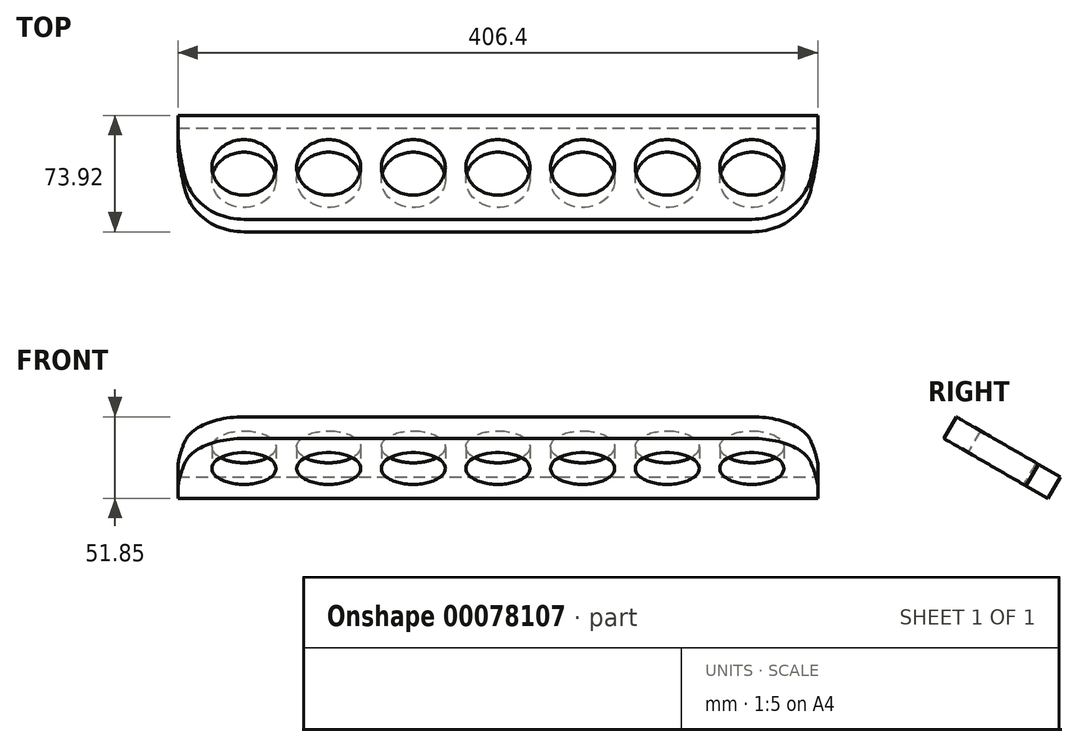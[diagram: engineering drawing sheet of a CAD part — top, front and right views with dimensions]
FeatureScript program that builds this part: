
annotation { "Feature Type Name" : "Feature", "Feature Type Description" : "" }
export const myFeature = defineFeature(function(context is Context, id is Id, definition is map)
    precondition{}
    {
        {
            assignVariable(context, id + "F0", {"name" : "panel_length", "anyValue" : 48});
        }
        {
            assignVariable(context, id + "F1", {"name" : "ply_thk", "anyValue" : 5 / 8});
        }
        {
            assignVariable(context, id + "F2", {"name" : "washer_thk", "anyValue" : 1 / 16});
        }
        {
            var Q0;
            Q0=qCreatedBy(makeId("Right.planeOp"),FACE);
            var sketch = newSketch(context, id + "F3", { "sketchPlane" : qUnion([Q0])});
            skCircle(sketch, "E0", {"center": v(0, 0) * mm, "radius": 254 * mm, "construction": true});
            skLineSegment(sketch, "E1", {"start": v(-651.77, -620.9) * mm, "end": v(0, 508) * mm, "construction": true});
            skCircle(sketch, "E2", {"center": v(0, 381) * mm, "radius": 63.5 * mm, "construction": true});
            skPoint(sketch, "E3", {"position": v(-219.97, 127) * mm});
            skPoint(sketch, "E4", {"position": v(-245.37, 83) * mm});
            skCircle(sketch, "E5", {"center": v(0, 254) * mm, "radius": 127 * mm, "construction": true});
            skLineSegment(sketch, "E6", {"start": v(-1219.2, 0) * mm, "end": v(1219.2, 0) * mm, "construction": true});
            skLineSegment(sketch, "E7", {"start": v(0, 1219.2) * mm, "end": v(0, -1219.2) * mm, "construction": true});
            skLineSegment(sketch, "E8", {"start": v(-245.37, 83) * mm, "end": v(-231.62, 75.07) * mm, "construction": true});
            skLineSegment(sketch, "E9", {"start": v(-231.62, 75.07) * mm, "end": v(-638.02, -628.84) * mm, "construction": true});
            skLineSegment(sketch, "E10", {"start": v(-638.02, -628.84) * mm, "end": v(-651.77, -620.9) * mm, "construction": true});
            skLineSegment(sketch, "E11", {"start": v(-231.62, 75.07) * mm, "end": v(-217.87, 67.13) * mm, "construction": true});
            skLineSegment(sketch, "E12", {"start": v(-217.87, 67.13) * mm, "end": v(-624.27, -636.77) * mm, "construction": true});
            skLineSegment(sketch, "E13", {"start": v(-624.27, -636.77) * mm, "end": v(-638.02, -628.84) * mm, "construction": true});
            skCircle(sketch, "E14", {"center": v(0, 0) * mm, "radius": 6.35 * mm, "construction": true});
            skCircle(sketch, "E15", {"center": v(0, 0) * mm, "radius": 9.53 * mm, "construction": true});
            skPoint(sketch, "E16", {"position": v(-55, 412.75) * mm});
            skPoint(sketch, "E17", {"position": v(-109.99, 317.5) * mm});
            skCircle(sketch, "E18", {"center": v(0, 0) * mm, "radius": 177.8 * mm, "construction": true});
            skCircle(sketch, "E19", {"center": v(0, 508) * mm, "radius": 6.35 * mm});
            skCircle(sketch, "E20", {"center": v(0, 508) * mm, "radius": 9.53 * mm});
            skCircle(sketch, "E21", {"center": v(0, 508) * mm, "radius": 12.7 * mm});
            skSolve(sketch);
        }
        {
            var Q0;
            Q0=qCreatedBy(makeId("Right.planeOp"),FACE);
            var sketch = newSketch(context, id + "F4", { "sketchPlane" : qUnion([Q0])});
            skArc(sketch, "E22", {"start": v(-98.09, -220.46) * mm, "mid": v(-82.53, -226.75) * mm, "end": v(-66.57, -231.93) * mm});
            skArc(sketch, "E23", {"start": v(-209.94, -413.28) * mm, "mid": v(-158.54, -435.6) * mm, "end": v(-104.83, -451.54) * mm});
            skArc(sketch, "E24", {"start": v(-248.13, -450.54) * mm, "mid": v(-175.92, -483.33) * mm, "end": v(-99.53, -504.63) * mm});
            skArc(sketch, "E25", {"start": v(-365.54, -639.5) * mm, "mid": v(-251.93, -692.18) * mm, "end": v(-131.05, -724.85) * mm});
            skLineSegment(sketch, "E26", {"start": v(160.85, -238.47) * mm, "end": v(229.05, -339.58) * mm});
            skLineSegment(sketch, "E27", {"start": v(-237.79, -697.16) * mm, "end": v(-166.04, -486.81) * mm, "construction": true});
            skLineSegment(sketch, "E28", {"start": v(-149.64, -438.73) * mm, "end": v(-77.9, -228.38) * mm, "construction": true});
            skLineSegment(sketch, "E29", {"start": v(30.07, -286.07) * mm, "end": v(42.82, -407.37) * mm});
            skLineSegment(sketch, "E30.0", {"start": v(0, 1219.2) * mm, "end": v(0, -1219.2) * mm, "construction": true});
            skLineSegment(sketch, "E31.MirrorCS", {"start": v(-30.07, -286.07) * mm, "end": v(-42.82, -407.37) * mm});
            skLineSegment(sketch, "E32.MirrorCS", {"start": v(-160.85, -238.47) * mm, "end": v(-229.05, -339.58) * mm});
            skLineSegment(sketch, "E33.0", {"start": v(-1219.2, 0) * mm, "end": v(1219.2, 0) * mm, "construction": true});
            skArc(sketch, "E34.trimOffspring", {"start": v(131.05, -724.85) * mm, "mid": v(251.93, -692.18) * mm, "end": v(365.54, -639.5) * mm});
            skArc(sketch, "E35.trimOffspring", {"start": v(99.53, -504.63) * mm, "mid": v(175.92, -483.33) * mm, "end": v(248.13, -450.54) * mm});
            skArc(sketch, "E36.trimOffspring", {"start": v(104.83, -451.54) * mm, "mid": v(158.54, -435.6) * mm, "end": v(209.94, -413.28) * mm});
            skArc(sketch, "E37.trimOffspring", {"start": v(66.57, -231.93) * mm, "mid": v(82.53, -226.75) * mm, "end": v(98.09, -220.46) * mm});
            skLineSegment(sketch, "E38.trimOffspring", {"start": v(58.84, -559.78) * mm, "end": v(71.49, -680.17) * mm});
            skLineSegment(sketch, "E39.trimOffspring", {"start": v(314.75, -466.63) * mm, "end": v(382.44, -567) * mm});
            skLineSegment(sketch, "E40.trimOffspring", {"start": v(-314.75, -466.63) * mm, "end": v(-382.44, -567) * mm});
            skLineSegment(sketch, "E41.trimOffspring", {"start": v(-58.84, -559.78) * mm, "end": v(-71.49, -680.17) * mm});
            skPoint(sketch, "E42.visualSharp", {"position": v(-134.93, -200.05) * mm});
            skArc(sketch, "E42.filletArc", {"start": v(-98.09, -220.46) * mm, "mid": v(-132.74, -218.05) * mm, "end": v(-160.85, -238.47) * mm});
            skPoint(sketch, "E43.visualSharp", {"position": v(-25.22, -239.98) * mm});
            skArc(sketch, "E43.filletArc", {"start": v(-30.07, -286.07) * mm, "mid": v(-38.47, -252.36) * mm, "end": v(-66.57, -231.93) * mm});
            skPoint(sketch, "E44.visualSharp", {"position": v(25.22, -239.98) * mm});
            skArc(sketch, "E44.filletArc", {"start": v(66.57, -231.93) * mm, "mid": v(38.47, -252.36) * mm, "end": v(30.07, -286.07) * mm});
            skPoint(sketch, "E45.visualSharp", {"position": v(134.93, -200.05) * mm});
            skArc(sketch, "E45.filletArc", {"start": v(160.85, -238.47) * mm, "mid": v(132.74, -218.05) * mm, "end": v(98.09, -220.46) * mm});
            skPoint(sketch, "E46.visualSharp", {"position": v(-259.21, -384.3) * mm});
            skArc(sketch, "E46.filletArc", {"start": v(-229.05, -339.58) * mm, "mid": v(-236.11, -380.74) * mm, "end": v(-209.94, -413.28) * mm});
            skPoint(sketch, "E47.visualSharp", {"position": v(-48.45, -461.01) * mm});
            skArc(sketch, "E47.filletArc", {"start": v(-104.83, -451.54) * mm, "mid": v(-63.86, -443.43) * mm, "end": v(-42.82, -407.37) * mm});
            skPoint(sketch, "E48.visualSharp", {"position": v(48.45, -461.01) * mm});
            skArc(sketch, "E48.filletArc", {"start": v(42.82, -407.37) * mm, "mid": v(63.86, -443.43) * mm, "end": v(104.83, -451.54) * mm});
            skPoint(sketch, "E49.visualSharp", {"position": v(259.21, -384.3) * mm});
            skArc(sketch, "E49.filletArc", {"start": v(209.94, -413.28) * mm, "mid": v(236.11, -380.74) * mm, "end": v(229.05, -339.58) * mm});
            skPoint(sketch, "E50.visualSharp", {"position": v(-411.9, -610.67) * mm});
            skArc(sketch, "E50.filletArc", {"start": v(-382.44, -567) * mm, "mid": v(-389.8, -606.93) * mm, "end": v(-365.54, -639.5) * mm});
            skPoint(sketch, "E51.visualSharp", {"position": v(-287.62, -426.42) * mm});
            skArc(sketch, "E51.filletArc", {"start": v(-248.13, -450.54) * mm, "mid": v(-284.56, -445.66) * mm, "end": v(-314.75, -466.63) * mm});
            skPoint(sketch, "E52.visualSharp", {"position": v(-53.76, -511.53) * mm});
            skArc(sketch, "E52.filletArc", {"start": v(-58.84, -559.78) * mm, "mid": v(-68.48, -524.3) * mm, "end": v(-99.53, -504.63) * mm});
            skPoint(sketch, "E53.visualSharp", {"position": v(-77, -732.56) * mm});
            skArc(sketch, "E53.filletArc", {"start": v(-131.05, -724.85) * mm, "mid": v(-91.53, -715.5) * mm, "end": v(-71.49, -680.17) * mm});
            skPoint(sketch, "E54.visualSharp", {"position": v(77, -732.56) * mm});
            skArc(sketch, "E54.filletArc", {"start": v(71.49, -680.17) * mm, "mid": v(91.53, -715.5) * mm, "end": v(131.05, -724.85) * mm});
            skPoint(sketch, "E55.visualSharp", {"position": v(53.76, -511.53) * mm});
            skArc(sketch, "E55.filletArc", {"start": v(99.53, -504.63) * mm, "mid": v(68.48, -524.3) * mm, "end": v(58.84, -559.78) * mm});
            skPoint(sketch, "E56.visualSharp", {"position": v(287.62, -426.42) * mm});
            skArc(sketch, "E56.filletArc", {"start": v(314.75, -466.63) * mm, "mid": v(284.56, -445.66) * mm, "end": v(248.13, -450.54) * mm});
            skPoint(sketch, "E57.visualSharp", {"position": v(411.9, -610.67) * mm});
            skArc(sketch, "E57.filletArc", {"start": v(365.54, -639.5) * mm, "mid": v(389.8, -606.93) * mm, "end": v(382.44, -567) * mm});
            skSolve(sketch);
        }
        {
            var Q0;
            Q0=makeQuery(id+"F3.imprint","IMPRINT",FACE,{"disambiguationData":[TD([[makeQuery(id+"F3.imprint","IMPRINT",EDGE,{"derivedFrom":sQuery(id+"F3.wireOp",EDGE,"E20")}),-1.0]])]});
            var Q1;
            Q1=makeQuery(id+"F3.imprint","IMPRINT",FACE,{"disambiguationData":[TD([[makeQuery(id+"F3.imprint","IMPRINT",EDGE,{"derivedFrom":sQuery(id+"F3.wireOp",EDGE,"E19")}),-1.0]])]});
            extrude(context, id + "F5", {"entities" : qUnion([Q0, Q1]), "depth" : (getVariable(context, 'washer_thk')) * mm});
        }
        {
            var Q0;
            Q0=makeQuery(id+"F3.imprint","IMPRINT",FACE,{"disambiguationData":[TD([[makeQuery(id+"F3.imprint","IMPRINT",EDGE,{"derivedFrom":sQuery(id+"F3.wireOp",EDGE,"E19")}),-1.0]])]});
            extrude(context, id + "F6", {"entities" : qUnion([Q0]), "depth" : (getVariable(context, 'ply_thk')) * mm});
        }
        {
            var Q0;
            Q0=makeQuery(id+"F3.imprint","IMPRINT",FACE,{"disambiguationData":[TD([[makeQuery(id+"F3.imprint","IMPRINT",EDGE,{"derivedFrom":sQuery(id+"F3.wireOp",EDGE,"E19")}),1.0]])]});
            extrude(context, id + "F7", {"entities" : qUnion([Q0]), "depth" : (getVariable(context, 'panel_length')) * mm});
        }
        {
            var Q0;
            Q0=qCreatedBy(makeId("Right.planeOp"),FACE);
            var sketch = newSketch(context, id + "F8", { "sketchPlane" : qUnion([Q0])});
            skCircle(sketch, "E58.0", {"center": v(0, 0) * mm, "radius": 254 * mm, "construction": true});
            skLineSegment(sketch, "E58.1", {"start": v(-217.87, 67.13) * mm, "end": v(-624.27, -636.77) * mm, "construction": true});
            skLineSegment(sketch, "E58.2", {"start": v(-231.62, 75.07) * mm, "end": v(-217.87, 67.13) * mm, "construction": true});
            skLineSegment(sketch, "E58.3", {"start": v(-231.62, 75.07) * mm, "end": v(-638.02, -628.84) * mm, "construction": true});
            skLineSegment(sketch, "E58.4", {"start": v(-624.27, -636.77) * mm, "end": v(-638.02, -628.84) * mm, "construction": true});
            skCircle(sketch, "E59", {"center": v(0, 0) * mm, "radius": 127 * mm, "construction": true});
            skCircle(sketch, "E60.0", {"center": v(0, 0) * mm, "radius": 177.8 * mm, "construction": true});
            skLineSegment(sketch, "E61", {"start": v(-212.37, 63.96) * mm, "end": v(-121.6, 36.62) * mm});
            skLineSegment(sketch, "E62", {"start": v(-212.37, 63.96) * mm, "end": v(-574.32, -562.96) * mm});
            skCircle(sketch, "E63", {"center": v(-535.83, -585.18) * mm, "radius": 44.45 * mm, "construction": true});
            skLineSegment(sketch, "E64.0", {"start": v(0, 1219.2) * mm, "end": v(0, -1219.2) * mm, "construction": true});
            skCircle(sketch, "E65", {"center": v(0, 0) * mm, "radius": 793.45 * mm, "construction": true});
            skCircle(sketch, "E66", {"center": v(-535.83, -585.18) * mm, "radius": 9.53 * mm, "construction": true});
            skCircle(sketch, "E67.MirrorC", {"center": v(455.1, -649.95) * mm, "radius": 44.45 * mm, "construction": true});
            skCircle(sketch, "E68.MirrorC", {"center": v(535.83, -585.18) * mm, "radius": 44.45 * mm, "construction": true});
            skCircle(sketch, "E69.MirrorC", {"center": v(455.1, -649.95) * mm, "radius": 9.53 * mm});
            skCircle(sketch, "E70.MirrorC", {"center": v(535.83, -585.18) * mm, "radius": 9.53 * mm, "construction": true});
            skLineSegment(sketch, "E71", {"start": v(-535.83, -585.18) * mm, "end": v(-421.53, -387.21) * mm, "construction": true});
            skLineSegment(sketch, "E72", {"start": v(-544.08, -580.42) * mm, "end": v(-429.78, -382.45) * mm});
            skCircle(sketch, "E73", {"center": v(-421.53, -387.21) * mm, "radius": 9.53 * mm, "construction": true});
            skLineSegment(sketch, "E74.MirrorCS", {"start": v(-527.58, -589.95) * mm, "end": v(-413.28, -391.97) * mm});
            skCircle(sketch, "E75", {"center": v(-218.33, -35.26) * mm, "radius": 44.45 * mm, "construction": true});
            skArc(sketch, "E76", {"start": v(-574.32, -562.96) * mm, "mid": v(-557.56, -623.96) * mm, "end": v(-496.78, -606.42) * mm});
            skArc(sketch, "E77", {"start": v(-496.78, -606.42) * mm, "mid": v(-51.13, -782.25) * mm, "end": v(413.62, -665.92) * mm});
            skArc(sketch, "E78", {"start": v(413.62, -665.92) * mm, "mid": v(473.92, -690.22) * mm, "end": v(493.97, -628.38) * mm});
            skArc(sketch, "E79", {"start": v(111.05, 61.63) * mm, "mid": v(-13.57, 126.27) * mm, "end": v(-121.6, 36.62) * mm});
            skArc(sketch, "E80", {"start": v(-544.08, -580.42) * mm, "mid": v(-540.6, -593.43) * mm, "end": v(-527.58, -589.95) * mm});
            skArc(sketch, "E81", {"start": v(-413.28, -391.97) * mm, "mid": v(-416.77, -378.96) * mm, "end": v(-429.78, -382.45) * mm});
            skCircle(sketch, "E82", {"center": v(-218.33, -35.26) * mm, "radius": 9.53 * mm});
            skCircle(sketch, "E83", {"center": v(0, 0) * mm, "radius": 9.53 * mm});
            skCircle(sketch, "E84", {"center": v(0, -127) * mm, "radius": 9.52 * mm, "construction": true});
            skCircle(sketch, "E85", {"center": v(0, 0) * mm, "radius": 837.9 * mm, "construction": true});
            skLineSegment(sketch, "E86", {"start": v(-1330.3, -888.7) * mm, "end": v(1330.3, -888.7) * mm, "construction": true});
            skPoint(sketch, "E87", {"position": v(0, -888.7) * mm});
            skCircle(sketch, "E88", {"center": v(63.5, -109.99) * mm, "radius": 9.53 * mm, "construction": true});
            skArc(sketch, "E89", {"start": v(0, -136.53) * mm, "mid": v(35.34, -131.87) * mm, "end": v(68.26, -118.23) * mm});
            skArc(sketch, "E90", {"start": v(0, -117.47) * mm, "mid": v(30.4, -113.47) * mm, "end": v(58.74, -101.74) * mm});
            skArc(sketch, "E91", {"start": v(0, -117.47) * mm, "mid": v(-9.52, -127) * mm, "end": v(0, -136.53) * mm});
            skArc(sketch, "E92", {"start": v(68.26, -118.23) * mm, "mid": v(71.75, -105.22) * mm, "end": v(58.74, -101.74) * mm});
            skLineSegment(sketch, "E93", {"start": v(493.97, -628.38) * mm, "end": v(111.05, 61.63) * mm});
            skCircle(sketch, "E94.MirrorC", {"center": v(218.33, -35.26) * mm, "radius": 9.53 * mm, "construction": true});
            skCircle(sketch, "E95.MirrorC", {"center": v(421.53, -387.21) * mm, "radius": 9.53 * mm, "construction": true});
            skLineSegment(sketch, "E96", {"start": v(0, 0) * mm, "end": v(63.5, -109.99) * mm, "construction": true});
            skCircle(sketch, "E97", {"center": v(0, -793.45) * mm, "radius": 6.35 * mm, "construction": true});
            skLineSegment(sketch, "E98", {"start": v(0, 0) * mm, "end": v(69.15, -790.43) * mm, "construction": true});
            skLineSegment(sketch, "E99", {"start": v(0, 0) * mm, "end": v(455.1, -649.95) * mm, "construction": true});
            skCircle(sketch, "E100", {"center": v(69.15, -790.43) * mm, "radius": 44.45 * mm, "construction": true});
            skLineSegment(sketch, "E101", {"start": v(-143.55, 168.8) * mm, "end": v(-78.6, 99.75) * mm, "construction": true});
            skLineSegment(sketch, "E102", {"start": v(-78.6, 99.75) * mm, "end": v(0, 0) * mm, "construction": true});
            skLineSegment(sketch, "E103", {"start": v(-121.6, 36.62) * mm, "end": v(0, 0) * mm, "construction": true});
            skArc(sketch, "E104", {"start": v(82.97, 104.4) * mm, "mid": v(0, 133.35) * mm, "end": v(-82.97, 104.4) * mm});
            skLineSegment(sketch, "E105", {"start": v(-113.5, 136.86) * mm, "end": v(-82.97, 104.4) * mm});
            skLineSegment(sketch, "E106.MirrorCS", {"start": v(113.5, 136.86) * mm, "end": v(82.97, 104.4) * mm});
            skArc(sketch, "E107", {"start": v(113.5, 136.86) * mm, "mid": v(0, 177.8) * mm, "end": v(-113.5, 136.86) * mm});
            skCircle(sketch, "E108", {"center": v(-52.13, 146.57) * mm, "radius": 6.35 * mm});
            skArc(sketch, "E109", {"start": v(0, 155.57) * mm, "mid": v(-52.13, 146.57) * mm, "end": v(-98.24, 120.62) * mm, "construction": true});
            skCircle(sketch, "E110.MirrorC", {"center": v(52.13, 146.57) * mm, "radius": 6.35 * mm});
            skCircle(sketch, "E111", {"center": v(0, -793.45) * mm, "radius": 9.53 * mm, "construction": true});
            skLineSegment(sketch, "E112.2.0", {"start": v(-98.09, -220.46) * mm, "end": v(-98.09, -220.46) * mm});
            skLineSegment(sketch, "E112.3.0", {"start": v(-248.13, -450.54) * mm, "end": v(-248.13, -450.54) * mm});
            skArc(sketch, "E113.1.0", {"start": v(-66.57, -231.93) * mm, "mid": v(-82.53, -226.75) * mm, "end": v(-98.09, -220.46) * mm});
            skArc(sketch, "E113.1.1", {"start": v(-98.09, -220.46) * mm, "mid": v(-132.74, -218.05) * mm, "end": v(-160.85, -238.47) * mm});
            skLineSegment(sketch, "E113.1.2", {"start": v(-160.85, -238.47) * mm, "end": v(-229.05, -339.58) * mm});
            skArc(sketch, "E113.1.3", {"start": v(-229.05, -339.58) * mm, "mid": v(-236.11, -380.74) * mm, "end": v(-209.94, -413.28) * mm});
            skArc(sketch, "E113.1.4", {"start": v(-209.94, -413.28) * mm, "mid": v(-158.54, -435.6) * mm, "end": v(-104.83, -451.54) * mm});
            skArc(sketch, "E113.1.5", {"start": v(-104.83, -451.54) * mm, "mid": v(-63.86, -443.43) * mm, "end": v(-42.82, -407.37) * mm});
            skLineSegment(sketch, "E113.1.6", {"start": v(-42.82, -407.37) * mm, "end": v(-30.07, -286.07) * mm});
            skArc(sketch, "E113.1.7", {"start": v(-30.07, -286.07) * mm, "mid": v(-38.47, -252.36) * mm, "end": v(-66.57, -231.93) * mm});
            skLineSegment(sketch, "E113.2.0", {"start": v(229.05, -339.58) * mm, "end": v(160.85, -238.47) * mm});
            skArc(sketch, "E113.2.1", {"start": v(160.85, -238.47) * mm, "mid": v(132.74, -218.05) * mm, "end": v(98.09, -220.46) * mm});
            skArc(sketch, "E113.2.2", {"start": v(98.09, -220.46) * mm, "mid": v(82.53, -226.75) * mm, "end": v(66.57, -231.93) * mm});
            skArc(sketch, "E113.2.3", {"start": v(66.57, -231.93) * mm, "mid": v(38.47, -252.36) * mm, "end": v(30.07, -286.07) * mm});
            skLineSegment(sketch, "E113.2.4", {"start": v(30.07, -286.07) * mm, "end": v(42.82, -407.37) * mm});
            skArc(sketch, "E113.2.5", {"start": v(42.82, -407.37) * mm, "mid": v(63.86, -443.43) * mm, "end": v(104.83, -451.54) * mm});
            skArc(sketch, "E113.2.6", {"start": v(104.83, -451.54) * mm, "mid": v(158.54, -435.6) * mm, "end": v(209.94, -413.28) * mm});
            skArc(sketch, "E113.2.7", {"start": v(209.94, -413.28) * mm, "mid": v(236.11, -380.74) * mm, "end": v(229.05, -339.58) * mm});
            skArc(sketch, "E113.3.0", {"start": v(71.49, -680.17) * mm, "mid": v(91.53, -715.5) * mm, "end": v(131.05, -724.85) * mm});
            skArc(sketch, "E113.3.1", {"start": v(131.05, -724.85) * mm, "mid": v(231.68, -699.22) * mm, "end": v(327.7, -659.7) * mm});
            skLineSegment(sketch, "E113.3.3", {"start": v(373.43, -553.63) * mm, "end": v(314.75, -466.63) * mm});
            skArc(sketch, "E113.3.4", {"start": v(314.75, -466.63) * mm, "mid": v(284.56, -445.66) * mm, "end": v(248.13, -450.54) * mm});
            skArc(sketch, "E113.3.5", {"start": v(248.13, -450.54) * mm, "mid": v(202.04, -473) * mm, "end": v(153.94, -490.77) * mm});
            skLineSegment(sketch, "E113.3.7", {"start": v(60.51, -575.76) * mm, "end": v(71.49, -680.17) * mm});
            skLineSegment(sketch, "E114", {"start": v(154.76, -539.49) * mm, "end": v(345.6, -592.31) * mm});
            skLineSegment(sketch, "E115", {"start": v(323.18, -612.46) * mm, "end": v(92.55, -548.62) * mm});
            skArc(sketch, "E116", {"start": v(365.54, -639.5) * mm, "mid": v(388.99, -625.52) * mm, "end": v(411.9, -610.67) * mm, "construction": true});
            skLineSegment(sketch, "E117", {"start": v(382.44, -567) * mm, "end": v(411.9, -610.67) * mm, "construction": true});
            skArc(sketch, "E118", {"start": v(53.76, -511.53) * mm, "mid": v(76.72, -508.6) * mm, "end": v(99.53, -504.63) * mm, "construction": true});
            skLineSegment(sketch, "E119", {"start": v(53.76, -511.53) * mm, "end": v(58.84, -559.78) * mm, "construction": true});
            skPoint(sketch, "E120.newPointB", {"position": v(365.54, -639.5) * mm});
            skArc(sketch, "E120.filletArc", {"start": v(327.7, -659.7) * mm, "mid": v(341.68, -634.52) * mm, "end": v(323.18, -612.46) * mm});
            skPoint(sketch, "E121.newPointB", {"position": v(382.44, -567) * mm});
            skArc(sketch, "E121.filletArc", {"start": v(345.6, -592.31) * mm, "mid": v(372.99, -582.67) * mm, "end": v(373.43, -553.63) * mm});
            skPoint(sketch, "E122.newPointB", {"position": v(99.53, -504.63) * mm});
            skArc(sketch, "E122.filletArc", {"start": v(153.94, -490.77) * mm, "mid": v(136.14, -515.44) * mm, "end": v(154.76, -539.49) * mm});
            skPoint(sketch, "E123.newPointB", {"position": v(58.84, -559.78) * mm});
            skArc(sketch, "E123.filletArc", {"start": v(92.55, -548.62) * mm, "mid": v(69.36, -553.72) * mm, "end": v(60.51, -575.76) * mm});
            skLineSegment(sketch, "E124", {"start": v(53.76, -511.53) * mm, "end": v(411.9, -610.67) * mm, "construction": true});
            skArc(sketch, "E125.MirrorCS", {"start": v(-92.55, -548.62) * mm, "mid": v(-69.36, -553.72) * mm, "end": v(-60.51, -575.76) * mm});
            skLineSegment(sketch, "E126.MirrorCS", {"start": v(-60.51, -575.76) * mm, "end": v(-71.49, -680.17) * mm});
            skArc(sketch, "E127.MirrorCS", {"start": v(-71.49, -680.17) * mm, "mid": v(-91.53, -715.5) * mm, "end": v(-131.05, -724.85) * mm});
            skArc(sketch, "E128.MirrorCS", {"start": v(-131.05, -724.85) * mm, "mid": v(-231.68, -699.22) * mm, "end": v(-327.7, -659.7) * mm});
            skArc(sketch, "E129.MirrorCS", {"start": v(-327.7, -659.7) * mm, "mid": v(-341.68, -634.52) * mm, "end": v(-323.18, -612.46) * mm});
            skLineSegment(sketch, "E130.MirrorCS", {"start": v(-323.18, -612.46) * mm, "end": v(-92.55, -548.62) * mm});
            skArc(sketch, "E131.MirrorCS", {"start": v(-153.94, -490.77) * mm, "mid": v(-136.14, -515.44) * mm, "end": v(-154.76, -539.49) * mm});
            skArc(sketch, "E132.MirrorCS", {"start": v(-248.13, -450.54) * mm, "mid": v(-202.04, -473) * mm, "end": v(-153.94, -490.77) * mm});
            skArc(sketch, "E133.MirrorCS", {"start": v(-314.75, -466.63) * mm, "mid": v(-284.56, -445.66) * mm, "end": v(-248.13, -450.54) * mm});
            skLineSegment(sketch, "E134.MirrorCS", {"start": v(-373.43, -553.63) * mm, "end": v(-314.75, -466.63) * mm});
            skArc(sketch, "E135.MirrorCS", {"start": v(-345.6, -592.31) * mm, "mid": v(-372.99, -582.67) * mm, "end": v(-373.43, -553.63) * mm});
            skLineSegment(sketch, "E136.MirrorCS", {"start": v(-154.76, -539.49) * mm, "end": v(-345.6, -592.31) * mm});
            skSolve(sketch);
        }
        {
            var Q0;
            Q0=qCreatedBy(makeId("Right.planeOp"),FACE);
            var sketch = newSketch(context, id + "F9", { "sketchPlane" : qUnion([Q0])});
            skCircle(sketch, "E137.0", {"center": v(-535.83, -585.18) * mm, "radius": 9.53 * mm, "construction": true});
            skCircle(sketch, "E137.1", {"center": v(-421.53, -387.21) * mm, "radius": 9.53 * mm, "construction": true});
            skCircle(sketch, "E137.2", {"center": v(0, -793.45) * mm, "radius": 9.53 * mm, "construction": true});
            skCircle(sketch, "E137.3", {"center": v(0, -127) * mm, "radius": 9.52 * mm, "construction": true});
            skCircle(sketch, "E137.4", {"center": v(63.5, -109.99) * mm, "radius": 9.53 * mm, "construction": true});
            skCircle(sketch, "E137.5", {"center": v(455.1, -649.95) * mm, "radius": 9.53 * mm, "construction": true});
            skCircle(sketch, "E137.6", {"center": v(69.15, -790.43) * mm, "radius": 44.45 * mm, "construction": true});
            skCircle(sketch, "E138.0", {"center": v(-218.33, -35.26) * mm, "radius": 9.53 * mm, "construction": true});
            skCircle(sketch, "E139", {"center": v(0, -793.45) * mm, "radius": 25.4 * mm, "construction": true});
            skCircle(sketch, "E140", {"center": v(69.15, -790.43) * mm, "radius": 25.4 * mm, "construction": true});
            skCircle(sketch, "E141", {"center": v(455.1, -649.95) * mm, "radius": 25.4 * mm, "construction": true});
            skCircle(sketch, "E142", {"center": v(-535.83, -585.18) * mm, "radius": 25.4 * mm, "construction": true});
            skCircle(sketch, "E143", {"center": v(-421.53, -387.21) * mm, "radius": 25.4 * mm, "construction": true});
            skCircle(sketch, "E144", {"center": v(-218.33, -35.26) * mm, "radius": 25.4 * mm, "construction": true});
            skCircle(sketch, "E145", {"center": v(0, -127) * mm, "radius": 25.4 * mm, "construction": true});
            skCircle(sketch, "E146", {"center": v(63.5, -109.99) * mm, "radius": 25.4 * mm, "construction": true});
            skLineSegment(sketch, "E147", {"start": v(-25.4, -127) * mm, "end": v(-25.4, -793.45) * mm});
            skCircle(sketch, "E148.0", {"center": v(0, 0) * mm, "radius": 127 * mm, "construction": true});
            skArc(sketch, "E149", {"start": v(0, -101.6) * mm, "mid": v(26.3, -98.14) * mm, "end": v(50.8, -87.99) * mm});
            skArc(sketch, "E150", {"start": v(0, -101.6) * mm, "mid": v(-17.96, -109.04) * mm, "end": v(-25.4, -127) * mm});
            skLineSegment(sketch, "E151", {"start": v(85.5, -97.29) * mm, "end": v(405.8, -652.08) * mm});
            skArc(sketch, "E152", {"start": v(85.5, -97.29) * mm, "mid": v(70.07, -85.45) * mm, "end": v(50.8, -87.99) * mm});
            skArc(sketch, "E153", {"start": v(0, -818.85) * mm, "mid": v(246.23, -780.95) * mm, "end": v(469.67, -670.76) * mm});
            skArc(sketch, "E154", {"start": v(-25.4, -793.45) * mm, "mid": v(-17.96, -811.4) * mm, "end": v(0, -818.85) * mm});
            skArc(sketch, "E155", {"start": v(405.8, -652.08) * mm, "mid": v(423.33, -640.85) * mm, "end": v(440.53, -629.15) * mm});
            skArc(sketch, "E156", {"start": v(469.67, -670.76) * mm, "mid": v(475.9, -635.38) * mm, "end": v(440.53, -629.15) * mm});
            skCircle(sketch, "E157", {"center": v(0, 0) * mm, "radius": 25.4 * mm, "construction": true});
            skLineSegment(sketch, "E158", {"start": v(-4.05, 25.08) * mm, "end": v(-222.38, -10.18) * mm});
            skLineSegment(sketch, "E159", {"start": v(-240.33, -22.56) * mm, "end": v(-557.83, -572.48) * mm});
            skLineSegment(sketch, "E160", {"start": v(-513.83, -597.88) * mm, "end": v(-202.37, -58.4) * mm});
            skLineSegment(sketch, "E161", {"start": v(-202.37, -58.4) * mm, "end": v(4.05, -25.08) * mm});
            skArc(sketch, "E162", {"start": v(4.05, -25.08) * mm, "mid": v(25.08, 4.05) * mm, "end": v(-4.05, 25.08) * mm});
            skArc(sketch, "E163", {"start": v(-222.38, -10.18) * mm, "mid": v(-232.75, -14.35) * mm, "end": v(-240.33, -22.56) * mm});
            skArc(sketch, "E164", {"start": v(-557.83, -572.48) * mm, "mid": v(-548.53, -607.18) * mm, "end": v(-513.83, -597.88) * mm});
            skLineSegment(sketch, "E165", {"start": v(-224.28, -33.03) * mm, "end": v(-446.94, -627.3) * mm, "construction": true});
            skLineSegment(sketch, "E166", {"start": v(-464.78, -620.6) * mm, "end": v(-429.1, -633.98) * mm});
            skCircle(sketch, "E167", {"center": v(-494.5, -656.65) * mm, "radius": 38.1 * mm, "construction": true});
            skLineSegment(sketch, "E168", {"start": v(-429.1, -633.98) * mm, "end": v(-424.98, -658.73) * mm});
            skLineSegment(sketch, "E169", {"start": v(-443.98, -601.28) * mm, "end": v(-398.3, -479.38) * mm});
            skLineSegment(sketch, "E170", {"start": v(-386.4, -483.84) * mm, "end": v(-432.08, -605.74) * mm});
            skLineSegment(sketch, "E171", {"start": v(-443.98, -601.28) * mm, "end": v(-441.6, -602.17) * mm});
            skLineSegment(sketch, "E172", {"start": v(-441.6, -602.17) * mm, "end": v(-450.5, -625.96) * mm});
            skLineSegment(sketch, "E173", {"start": v(-443.37, -628.63) * mm, "end": v(-434.46, -604.85) * mm});
            skLineSegment(sketch, "E174", {"start": v(-434.46, -604.85) * mm, "end": v(-432.08, -605.74) * mm});
            skLineSegment(sketch, "E175", {"start": v(-441.6, -602.17) * mm, "end": v(-438.03, -603.5) * mm, "construction": true});
            skLineSegment(sketch, "E176", {"start": v(-438.03, -603.5) * mm, "end": v(-434.46, -604.85) * mm, "construction": true});
            skLineSegment(sketch, "E177", {"start": v(-398.3, -479.38) * mm, "end": v(-395.92, -480.27) * mm});
            skLineSegment(sketch, "E178", {"start": v(-386.4, -483.84) * mm, "end": v(-388.79, -482.95) * mm});
            skLineSegment(sketch, "E179", {"start": v(-388.79, -482.95) * mm, "end": v(-384.33, -471.05) * mm});
            skLineSegment(sketch, "E180", {"start": v(-395.92, -480.27) * mm, "end": v(-391.47, -468.38) * mm});
            skCircle(sketch, "E181", {"center": v(-218.33, -35.26) * mm, "radius": 6.35 * mm, "construction": true});
            skCircle(sketch, "E182.0", {"center": v(0, -793.45) * mm, "radius": 6.35 * mm, "construction": true});
            skLineSegment(sketch, "E183", {"start": v(-6.27, -794.46) * mm, "end": v(-140.41, 33.57) * mm, "construction": true});
            skLineSegment(sketch, "E184", {"start": v(-159.22, 30.53) * mm, "end": v(-121.6, 36.62) * mm});
            skPoint(sketch, "E185", {"position": v(-446.94, -627.3) * mm});
            skLineSegment(sketch, "E186", {"start": v(-464.78, -620.6) * mm, "end": v(-471.58, -626.21) * mm});
            skLineSegment(sketch, "E187", {"start": v(-144.17, 32.97) * mm, "end": v(-117.77, -130) * mm});
            skLineSegment(sketch, "E188", {"start": v(-136.65, 34.18) * mm, "end": v(-110.25, -128.8) * mm});
            skLineSegment(sketch, "E189", {"start": v(-110.25, -128.8) * mm, "end": v(-107.74, -128.39) * mm});
            skLineSegment(sketch, "E190", {"start": v(-117.77, -130) * mm, "end": v(-120.28, -130.42) * mm});
            skLineSegment(sketch, "E191", {"start": v(-117.77, -130) * mm, "end": v(-114, -129.4) * mm, "construction": true});
            skLineSegment(sketch, "E192", {"start": v(-114, -129.4) * mm, "end": v(-110.25, -128.8) * mm, "construction": true});
            skLineSegment(sketch, "E193", {"start": v(-159.22, 30.53) * mm, "end": v(-178.05, 53.62) * mm});
            skLineSegment(sketch, "E194", {"start": v(-99.46, -258.92) * mm, "end": v(-120.28, -130.42) * mm});
            skLineSegment(sketch, "E195", {"start": v(-86.92, -256.88) * mm, "end": v(-107.74, -128.39) * mm});
            skLineSegment(sketch, "E196", {"start": v(-391.47, -468.38) * mm, "end": v(-395.03, -467.04) * mm});
            skLineSegment(sketch, "E197", {"start": v(-395.03, -467.04) * mm, "end": v(-339.33, -318.39) * mm});
            skLineSegment(sketch, "E198", {"start": v(-325.06, -323.73) * mm, "end": v(-380.76, -472.4) * mm});
            skLineSegment(sketch, "E199", {"start": v(-380.76, -472.4) * mm, "end": v(-384.33, -471.05) * mm});
            skLineSegment(sketch, "E200", {"start": v(-339.33, -318.39) * mm, "end": v(-335.77, -319.72) * mm});
            skLineSegment(sketch, "E201", {"start": v(-335.77, -319.72) * mm, "end": v(-303.47, -233.52) * mm});
            skLineSegment(sketch, "E202", {"start": v(-280.28, -193.37) * mm, "end": v(-328.63, -322.4) * mm});
            skLineSegment(sketch, "E203", {"start": v(-328.63, -322.4) * mm, "end": v(-325.06, -323.73) * mm});
            skLineSegment(sketch, "E204", {"start": v(-99.46, -258.92) * mm, "end": v(-96.95, -258.5) * mm});
            skLineSegment(sketch, "E205", {"start": v(-96.95, -258.5) * mm, "end": v(-94.92, -271.05) * mm});
            skLineSegment(sketch, "E206", {"start": v(-87.4, -269.83) * mm, "end": v(-89.43, -257.3) * mm});
            skLineSegment(sketch, "E207", {"start": v(-89.43, -257.3) * mm, "end": v(-86.92, -256.88) * mm});
            skLineSegment(sketch, "E208", {"start": v(-87.4, -269.83) * mm, "end": v(-83.64, -269.22) * mm});
            skLineSegment(sketch, "E209", {"start": v(-83.64, -269.22) * mm, "end": v(-58.25, -425.93) * mm});
            skLineSegment(sketch, "E210", {"start": v(-73.3, -428.36) * mm, "end": v(-98.68, -271.66) * mm});
            skLineSegment(sketch, "E211", {"start": v(-98.68, -271.66) * mm, "end": v(-94.92, -271.05) * mm});
            skLineSegment(sketch, "E212", {"start": v(-73.3, -428.36) * mm, "end": v(-69.53, -427.75) * mm});
            skLineSegment(sketch, "E213", {"start": v(-69.53, -427.75) * mm, "end": v(-25.4, -700.19) * mm});
            skLineSegment(sketch, "E214", {"start": v(-25.4, -652.54) * mm, "end": v(-62.01, -426.53) * mm});
            skLineSegment(sketch, "E215", {"start": v(-62.01, -426.53) * mm, "end": v(-58.25, -425.93) * mm});
            skArc(sketch, "E216", {"start": v(-471.58, -626.21) * mm, "mid": v(-471.07, -675.13) * mm, "end": v(-424.98, -658.73) * mm});
            skArc(sketch, "E217", {"start": v(-121.6, 36.62) * mm, "mid": v(-146.2, 57.17) * mm, "end": v(-178.05, 53.62) * mm});
            skSolve(sketch);
        }
        {
            var Q0;
            Q0=qCreatedBy(makeId("Right.planeOp"),FACE);
            var sketch = newSketch(context, id + "F10", { "sketchPlane" : qUnion([Q0])});
            skArc(sketch, "E218.0", {"start": v(82.6, -185.65) * mm, "mid": v(69.5, -190.95) * mm, "end": v(56.06, -195.31) * mm, "construction": true});
            skArc(sketch, "E218.1", {"start": v(192.44, -217.17) * mm, "mid": v(143.25, -181.43) * mm, "end": v(82.6, -185.65) * mm, "construction": true});
            skArc(sketch, "E218.2", {"start": v(56.06, -195.31) * mm, "mid": v(6.88, -231.06) * mm, "end": v(-7.82, -290.06) * mm, "construction": true});
            skLineSegment(sketch, "E218.3", {"start": v(260.64, -318.28) * mm, "end": v(192.44, -217.17) * mm, "construction": true});
            skLineSegment(sketch, "E218.4", {"start": v(-7.82, -290.06) * mm, "end": v(4.92, -411.35) * mm, "construction": true});
            skArc(sketch, "E218.5", {"start": v(4.92, -411.35) * mm, "mid": v(41.76, -474.46) * mm, "end": v(113.44, -488.66) * mm, "construction": true});
            skArc(sketch, "E218.6", {"start": v(113.44, -488.66) * mm, "mid": v(171.57, -471.4) * mm, "end": v(227.2, -447.25) * mm, "construction": true});
            skArc(sketch, "E218.7", {"start": v(227.2, -447.25) * mm, "mid": v(273, -390.3) * mm, "end": v(260.64, -318.28) * mm, "construction": true});
            skLineSegment(sketch, "E219.0", {"start": v(405.02, -532.33) * mm, "end": v(346.33, -445.33) * mm, "construction": true});
            skArc(sketch, "E219.1", {"start": v(229.75, -417.17) * mm, "mid": v(187.07, -437.97) * mm, "end": v(142.53, -454.42) * mm, "construction": true});
            skArc(sketch, "E219.2", {"start": v(142.53, -454.42) * mm, "mid": v(98.05, -516.09) * mm, "end": v(144.6, -576.2) * mm, "construction": true});
            skArc(sketch, "E219.3", {"start": v(346.33, -445.33) * mm, "mid": v(293.5, -408.63) * mm, "end": v(229.75, -417.17) * mm, "construction": true});
            skLineSegment(sketch, "E219.4", {"start": v(144.6, -576.2) * mm, "end": v(335.43, -629.03) * mm, "construction": true});
            skArc(sketch, "E219.5", {"start": v(335.43, -629.03) * mm, "mid": v(403.92, -604.92) * mm, "end": v(405.02, -532.33) * mm, "construction": true});
            skArc(sketch, "E220.0", {"start": v(344.65, -693.81) * mm, "mid": v(379.61, -630.89) * mm, "end": v(333.34, -575.74) * mm, "construction": true});
            skArc(sketch, "E220.1", {"start": v(102.72, -511.9) * mm, "mid": v(44.74, -524.65) * mm, "end": v(22.62, -579.74) * mm, "construction": true});
            skLineSegment(sketch, "E220.2", {"start": v(22.62, -579.74) * mm, "end": v(33.6, -684.15) * mm, "construction": true});
            skLineSegment(sketch, "E220.3", {"start": v(333.34, -575.74) * mm, "end": v(102.72, -511.9) * mm, "construction": true});
            skArc(sketch, "E220.4", {"start": v(33.6, -684.15) * mm, "mid": v(68.66, -745.97) * mm, "end": v(137.83, -762.34) * mm, "construction": true});
            skArc(sketch, "E220.5", {"start": v(137.83, -762.34) * mm, "mid": v(243.66, -735.38) * mm, "end": v(344.65, -693.81) * mm, "construction": true});
            skArc(sketch, "E221.0", {"start": v(0, -174.62) * mm, "mid": v(45.2, -168.67) * mm, "end": v(87.31, -151.23) * mm, "construction": true});
            skArc(sketch, "E221.1", {"start": v(0, -79.38) * mm, "mid": v(-47.62, -127) * mm, "end": v(0, -174.62) * mm, "construction": true});
            skArc(sketch, "E221.2", {"start": v(0, -79.38) * mm, "mid": v(20.54, -76.67) * mm, "end": v(39.69, -68.74) * mm, "construction": true});
            skArc(sketch, "E221.3", {"start": v(87.31, -151.23) * mm, "mid": v(104.74, -86.17) * mm, "end": v(39.69, -68.74) * mm, "construction": true});
            skCircle(sketch, "E222.0", {"center": v(0, 0) * mm, "radius": 47.62 * mm, "construction": true});
            skCircle(sketch, "E223.0", {"center": v(-218.33, -35.26) * mm, "radius": 47.62 * mm, "construction": true});
            skArc(sketch, "E224.0", {"start": v(-516.14, -538.38) * mm, "mid": v(-51.5, -744.04) * mm, "end": v(437.05, -604.34) * mm, "construction": true});
            skLineSegment(sketch, "E225.0", {"start": v(-194.47, 18.77) * mm, "end": v(-516.14, -538.38) * mm, "construction": true});
            skLineSegment(sketch, "E226.0", {"start": v(437.05, -604.34) * mm, "end": v(77.73, 43.14) * mm, "construction": true});
            skArc(sketch, "E226.1", {"start": v(77.73, 43.14) * mm, "mid": v(-28.68, 84.15) * mm, "end": v(-87.9, -13.32) * mm, "construction": true});
            skLineSegment(sketch, "E226.2", {"start": v(-194.47, 18.77) * mm, "end": v(-87.9, -13.32) * mm, "construction": true});
            skArc(sketch, "E227.0", {"start": v(-380.29, -411.02) * mm, "mid": v(-397.72, -345.97) * mm, "end": v(-462.77, -363.4) * mm, "construction": true});
            skLineSegment(sketch, "E227.1", {"start": v(-494.59, -609) * mm, "end": v(-380.29, -411.02) * mm, "construction": true});
            skArc(sketch, "E227.2", {"start": v(-577.07, -561.37) * mm, "mid": v(-559.64, -626.43) * mm, "end": v(-494.59, -609) * mm, "construction": true});
            skLineSegment(sketch, "E227.3", {"start": v(-577.07, -561.37) * mm, "end": v(-462.77, -363.4) * mm, "construction": true});
            skLineSegment(sketch, "E228.0", {"start": v(0, 1219.2) * mm, "end": v(0, -1219.2) * mm, "construction": true});
            skArc(sketch, "E229.MirrorCS", {"start": v(-4.92, -411.35) * mm, "mid": v(-41.76, -474.46) * mm, "end": v(-113.44, -488.66) * mm, "construction": true});
            skArc(sketch, "E230.MirrorCS", {"start": v(-113.44, -488.66) * mm, "mid": v(-171.57, -471.4) * mm, "end": v(-227.2, -447.25) * mm, "construction": true});
            skArc(sketch, "E231.MirrorCS", {"start": v(-227.2, -447.25) * mm, "mid": v(-273, -390.3) * mm, "end": v(-260.64, -318.28) * mm, "construction": true});
            skLineSegment(sketch, "E232.MirrorCS", {"start": v(-260.64, -318.28) * mm, "end": v(-192.44, -217.17) * mm, "construction": true});
            skArc(sketch, "E233.MirrorCS", {"start": v(-192.44, -217.17) * mm, "mid": v(-143.25, -181.43) * mm, "end": v(-82.6, -185.65) * mm, "construction": true});
            skArc(sketch, "E234.MirrorCS", {"start": v(-82.6, -185.65) * mm, "mid": v(-69.5, -190.95) * mm, "end": v(-56.06, -195.31) * mm, "construction": true});
            skArc(sketch, "E235.MirrorCS", {"start": v(-56.06, -195.31) * mm, "mid": v(-6.88, -231.06) * mm, "end": v(7.82, -290.06) * mm, "construction": true});
            skLineSegment(sketch, "E236.MirrorCS", {"start": v(7.82, -290.06) * mm, "end": v(-4.92, -411.35) * mm, "construction": true});
            skArc(sketch, "E237.MirrorCS", {"start": v(-142.53, -454.42) * mm, "mid": v(-98.05, -516.09) * mm, "end": v(-144.6, -576.2) * mm, "construction": true});
            skArc(sketch, "E238.MirrorCS", {"start": v(-229.75, -417.17) * mm, "mid": v(-187.07, -437.97) * mm, "end": v(-142.53, -454.42) * mm, "construction": true});
            skArc(sketch, "E239.MirrorCS", {"start": v(-346.33, -445.33) * mm, "mid": v(-293.5, -408.63) * mm, "end": v(-229.75, -417.17) * mm, "construction": true});
            skLineSegment(sketch, "E240.MirrorCS", {"start": v(-405.02, -532.33) * mm, "end": v(-346.33, -445.33) * mm, "construction": true});
            skArc(sketch, "E241.MirrorCS", {"start": v(-335.43, -629.03) * mm, "mid": v(-403.92, -604.92) * mm, "end": v(-405.02, -532.33) * mm, "construction": true});
            skLineSegment(sketch, "E242.MirrorCS", {"start": v(-144.6, -576.2) * mm, "end": v(-335.43, -629.03) * mm, "construction": true});
            skLineSegment(sketch, "E243.MirrorCS", {"start": v(-333.34, -575.74) * mm, "end": v(-102.72, -511.9) * mm, "construction": true});
            skArc(sketch, "E244.MirrorCS", {"start": v(-344.65, -693.81) * mm, "mid": v(-379.61, -630.89) * mm, "end": v(-333.34, -575.74) * mm, "construction": true});
            skArc(sketch, "E245.MirrorCS", {"start": v(-137.83, -762.34) * mm, "mid": v(-243.66, -735.38) * mm, "end": v(-344.65, -693.81) * mm, "construction": true});
            skArc(sketch, "E246.MirrorCS", {"start": v(-33.6, -684.15) * mm, "mid": v(-68.66, -745.97) * mm, "end": v(-137.83, -762.34) * mm, "construction": true});
            skLineSegment(sketch, "E247.MirrorCS", {"start": v(-22.62, -579.74) * mm, "end": v(-33.6, -684.15) * mm, "construction": true});
            skArc(sketch, "E248.MirrorCS", {"start": v(-102.72, -511.9) * mm, "mid": v(-44.74, -524.65) * mm, "end": v(-22.62, -579.74) * mm, "construction": true});
            skCircle(sketch, "E249", {"center": v(-256.1, -206) * mm, "radius": 59.02 * mm});
            skCircle(sketch, "E250", {"center": v(-329.12, -340.5) * mm, "radius": 55.92 * mm});
            skCircle(sketch, "E251", {"center": v(-118.99, -104.5) * mm, "radius": 73.47 * mm});
            skCircle(sketch, "E252", {"center": v(77.51, -28.57) * mm, "radius": 34.99 * mm});
            skCircle(sketch, "E253", {"center": v(140.14, -143.72) * mm, "radius": 36.1 * mm});
            skCircle(sketch, "E254", {"center": v(0, -502.05) * mm, "radius": 47.88 * mm});
            skCircle(sketch, "E255", {"center": v(0, -708.23) * mm, "radius": 37.6 * mm});
            skCircle(sketch, "E256", {"center": v(0, -199.9) * mm, "radius": 25.27 * mm});
            skCircle(sketch, "E257", {"center": v(294.07, -388.15) * mm, "radius": 20.12 * mm});
            skCircle(sketch, "E258", {"center": v(-441.62, -568.75) * mm, "radius": 25.75 * mm});
            skCircle(sketch, "E259", {"center": v(-375.27, -447.68) * mm, "radius": 22.67 * mm});
            skSolve(sketch);
        }
        {
            var Q0;
            Q0=makeQuery(id+"F8.imprint","IMPRINT",FACE,{"disambiguationData":[TD([[makeQuery(id+"F8.imprint","IMPRINT",EDGE,{"derivedFrom":sQuery(id+"F8.wireOp",EDGE,"E61")}),-1.0]])]});
            extrude(context, id + "F11", {"entities" : qUnion([Q0]), "depth" : (getVariable(context, 'ply_thk')) * mm});
        }
        {
            var Q0;
            Q0=makeQuery(id+"F8.imprint","IMPRINT",FACE,{"disambiguationData":[TD([[makeQuery(id+"F8.imprint","IMPRINT",EDGE,{"derivedFrom":sQuery(id+"F8.wireOp",EDGE,"E61")}),-1.0]])]});
            extrude(context, id + "F12", {"entities" : qUnion([Q0]), "oppositeDirection" : true, "depth" : (getVariable(context, 'ply_thk')) * mm});
        }
        {
            var Q0;
            Q0=makeQuery(id+"F10.imprint","IMPRINT",FACE,{"disambiguationData":[TD([[makeQuery(id+"F10.imprint","IMPRINT",EDGE,{"derivedFrom":sQuery(id+"F10.wireOp",EDGE,"E255")}),1.0]])]});
            var Q1;
            Q1=makeQuery(id+"F10.imprint","IMPRINT",FACE,{"disambiguationData":[TD([[makeQuery(id+"F10.imprint","IMPRINT",EDGE,{"derivedFrom":sQuery(id+"F10.wireOp",EDGE,"E254")}),1.0]])]});
            var Q2;
            Q2=makeQuery(id+"F10.imprint","IMPRINT",FACE,{"disambiguationData":[TD([[makeQuery(id+"F10.imprint","IMPRINT",EDGE,{"derivedFrom":sQuery(id+"F10.wireOp",EDGE,"E250")}),1.0]])]});
            var Q3;
            Q3=makeQuery(id+"F10.imprint","IMPRINT",FACE,{"disambiguationData":[TD([[makeQuery(id+"F10.imprint","IMPRINT",EDGE,{"derivedFrom":sQuery(id+"F10.wireOp",EDGE,"E249")}),1.0]])]});
            var Q4;
            Q4=makeQuery(id+"F10.imprint","IMPRINT",FACE,{"disambiguationData":[TD([[makeQuery(id+"F10.imprint","IMPRINT",EDGE,{"derivedFrom":sQuery(id+"F10.wireOp",EDGE,"E251")}),1.0]])]});
            var Q5;
            Q5=makeQuery(id+"F10.imprint","IMPRINT",FACE,{"disambiguationData":[TD([[makeQuery(id+"F10.imprint","IMPRINT",EDGE,{"derivedFrom":sQuery(id+"F10.wireOp",EDGE,"E256")}),1.0]])]});
            var Q6;
            Q6=makeQuery(id+"F10.imprint","IMPRINT",FACE,{"disambiguationData":[TD([[makeQuery(id+"F10.imprint","IMPRINT",EDGE,{"derivedFrom":sQuery(id+"F10.wireOp",EDGE,"E253")}),1.0]])]});
            var Q7;
            Q7=makeQuery(id+"F10.imprint","IMPRINT",FACE,{"disambiguationData":[TD([[makeQuery(id+"F10.imprint","IMPRINT",EDGE,{"derivedFrom":sQuery(id+"F10.wireOp",EDGE,"E252")}),1.0]])]});
            var Q8;
            Q8=makeQuery(id+"F10.imprint","IMPRINT",FACE,{"disambiguationData":[TD([[makeQuery(id+"F10.imprint","IMPRINT",EDGE,{"derivedFrom":sQuery(id+"F10.wireOp",EDGE,"E257")}),1.0]])]});
            var Q9;
            Q9=makeQuery(id+"F10.imprint","IMPRINT",FACE,{"disambiguationData":[TD([[makeQuery(id+"F10.imprint","IMPRINT",EDGE,{"derivedFrom":sQuery(id+"F10.wireOp",EDGE,"E258")}),1.0]])]});
            var Q10;
            Q10=makeQuery(id+"F10.imprint","IMPRINT",FACE,{"disambiguationData":[TD([[makeQuery(id+"F10.imprint","IMPRINT",EDGE,{"derivedFrom":sQuery(id+"F10.wireOp",EDGE,"E259")}),1.0]])]});
            extrude(context, id + "F13", {"entities" : qUnion([Q0, Q1, Q2, Q3, Q4, Q5, Q6, Q7, Q8, Q9, Q10]), "operationType" : NewBodyOperationType.REMOVE, "endBound" : BoundingType.SYMMETRIC, "depth" : 50.8 * mm});
        }
        {
            var Q0;
            Q0=makeQuery(id+"F11.opExtrude","SWEPT_EDGE",EDGE,{"disambiguationData":[OSD([sQuery(id+"F8.wireOp",EDGE,"E76"),sQuery(id+"F8.wireOp",EDGE,"E77")])]});
            var Q1;
            Q1=makeQuery(id+"F11.opExtrude","SWEPT_EDGE",EDGE,{"disambiguationData":[OSD([sQuery(id+"F8.wireOp",EDGE,"E77"),sQuery(id+"F8.wireOp",EDGE,"E78")])]});
            var Q2;
            Q2=makeQuery(id+"F12.opExtrude","SWEPT_EDGE",EDGE,{"disambiguationData":[OSD([sQuery(id+"F8.wireOp",EDGE,"E76"),sQuery(id+"F8.wireOp",EDGE,"E77")])]});
            var Q3;
            Q3=makeQuery(id+"F12.opExtrude","SWEPT_EDGE",EDGE,{"disambiguationData":[OSD([sQuery(id+"F8.wireOp",EDGE,"E77"),sQuery(id+"F8.wireOp",EDGE,"E78")])]});
            fillet(context, id + "F14", {"entities" : qUnion([Q0, Q1, Q2, Q3]), "radius" : 25.4 * mm, "tangentPropagation" : true, "allowEdgeOverflow" : false});
        }
        {
            var Q0;
            Q0=makeQuery(id+"F9.imprint","IMPRINT",FACE,{"disambiguationData":[TD([[makeQuery(id+"F9.imprint","IMPRINT",EDGE,{"derivedFrom":sQuery(id+"F9.wireOp",EDGE,"E159")}),1.0]])]});
            var Q1;
            {var subQ0=sQuery(id+"F9.wireOp",EDGE,"E168");Q1=makeQuery(id+"F9.imprint","IMPRINT",FACE,{"disambiguationData":[TD([[makeQuery(id+"F9.imprint","IMPRINT",EDGE,{"derivedFrom":subQ0}),-1.0]])]});}
            var Q2;
            Q2=makeQuery(id+"F9.imprint","IMPRINT",FACE,{"disambiguationData":[TD([[makeQuery(id+"F9.imprint","IMPRINT",EDGE,{"derivedFrom":sQuery(id+"F9.wireOp",EDGE,"E169")}),-1.0]])]});
            var Q3;
            {var subQ1=sQuery(id+"F9.wireOp",EDGE,"E189");Q3=makeQuery(id+"F9.imprint","IMPRINT",FACE,{"disambiguationData":[TD([[makeQuery(id+"F9.imprint","IMPRINT",EDGE,{"derivedFrom":subQ1}),-1.0]])]});}
            var Q4;
            Q4=makeQuery(id+"F9.imprint","IMPRINT",FACE,{"disambiguationData":[TD([[makeQuery(id+"F9.imprint","IMPRINT",EDGE,{"derivedFrom":sQuery(id+"F9.wireOp",EDGE,"E149")}),-1.0]])]});
            var Q5;
            {var subQ0=sQuery(id+"F9.wireOp",EDGE,"E193");Q5=makeQuery(id+"F9.imprint","IMPRINT",FACE,{"disambiguationData":[TD([[makeQuery(id+"F9.imprint","IMPRINT",EDGE,{"derivedFrom":subQ0}),-1.0]])]});}
            var Q6;
            {var subQ0=sQuery(id+"F9.wireOp",EDGE,"E162");Q6=makeQuery(id+"F9.imprint","IMPRINT",FACE,{"disambiguationData":[TD([[makeQuery(id+"F9.imprint","IMPRINT",EDGE,{"derivedFrom":subQ0}),1.0]])]});}
            var Q7;
            {var subQ0=sQuery(id+"F9.wireOp",EDGE,"E188");var subQ1=sQuery(id+"F9.wireOp",EDGE,"E158");var subQ2=makeQuery(id+"F9.imprint","INTERSECT",VERTEX,{"derivedFrom":[subQ1,subQ0]});Q7=makeQuery(id+"F9.imprint","IMPRINT",FACE,{"disambiguationData":[TD([[makeQuery(id+"F9.imprint","IMPRINT",EDGE,{"disambiguationData":[TD([[subQ2,-1.0]])],"derivedFrom":subQ1}),1.0]])]});}
            var Q8;
            {var subQ0=sQuery(id+"F9.wireOp",EDGE,"E188");var subQ1=sQuery(id+"F9.wireOp",EDGE,"E158");var subQ2=makeQuery(id+"F9.imprint","INTERSECT",VERTEX,{"derivedFrom":[subQ1,subQ0]});Q8=makeQuery(id+"F9.imprint","IMPRINT",FACE,{"disambiguationData":[TD([[makeQuery(id+"F9.imprint","IMPRINT",EDGE,{"disambiguationData":[TD([[subQ2,-1.0]])],"derivedFrom":subQ1}),-1.0]])]});}
            var Q9;
            Q9=makeQuery(id+"F12.opExtrude","CAP_FACE",FACE,{"disambiguationData":[OSD([sQuery(id+"F8.wireOp",EDGE,"E61"),sQuery(id+"F8.wireOp",EDGE,"E62"),sQuery(id+"F8.wireOp",EDGE,"E69.MirrorC"),sQuery(id+"F8.wireOp",EDGE,"E72"),sQuery(id+"F8.wireOp",EDGE,"E74.MirrorCS"),sQuery(id+"F8.wireOp",EDGE,"E76"),sQuery(id+"F8.wireOp",EDGE,"E77"),sQuery(id+"F8.wireOp",EDGE,"E78"),sQuery(id+"F8.wireOp",EDGE,"E79"),sQuery(id+"F8.wireOp",EDGE,"E80"),sQuery(id+"F8.wireOp",EDGE,"E81"),sQuery(id+"F8.wireOp",EDGE,"E82"),sQuery(id+"F8.wireOp",EDGE,"E83"),sQuery(id+"F8.wireOp",EDGE,"E89"),sQuery(id+"F8.wireOp",EDGE,"E90"),sQuery(id+"F8.wireOp",EDGE,"E91"),sQuery(id+"F8.wireOp",EDGE,"E92"),sQuery(id+"F8.wireOp",EDGE,"E93"),sQuery(id+"F8.wireOp",EDGE,"E113.1.0"),sQuery(id+"F8.wireOp",EDGE,"E113.1.1"),sQuery(id+"F8.wireOp",EDGE,"E113.1.2"),sQuery(id+"F8.wireOp",EDGE,"E113.1.3"),sQuery(id+"F8.wireOp",EDGE,"E113.1.4"),sQuery(id+"F8.wireOp",EDGE,"E113.1.5"),sQuery(id+"F8.wireOp",EDGE,"E113.1.6"),sQuery(id+"F8.wireOp",EDGE,"E113.1.7"),sQuery(id+"F8.wireOp",EDGE,"E113.2.0"),sQuery(id+"F8.wireOp",EDGE,"E113.2.1"),sQuery(id+"F8.wireOp",EDGE,"E113.2.2"),sQuery(id+"F8.wireOp",EDGE,"E113.2.3"),sQuery(id+"F8.wireOp",EDGE,"E113.2.4"),sQuery(id+"F8.wireOp",EDGE,"E113.2.5"),sQuery(id+"F8.wireOp",EDGE,"E113.2.6"),sQuery(id+"F8.wireOp",EDGE,"E113.2.7"),sQuery(id+"F8.wireOp",EDGE,"E113.3.0"),sQuery(id+"F8.wireOp",EDGE,"E113.3.1"),sQuery(id+"F8.wireOp",EDGE,"E113.3.3"),sQuery(id+"F8.wireOp",EDGE,"E113.3.4"),sQuery(id+"F8.wireOp",EDGE,"E113.3.5"),sQuery(id+"F8.wireOp",EDGE,"E113.3.7"),sQuery(id+"F8.wireOp",EDGE,"E114"),sQuery(id+"F8.wireOp",EDGE,"E115"),sQuery(id+"F8.wireOp",EDGE,"E120.filletArc"),sQuery(id+"F8.wireOp",EDGE,"E121.filletArc"),sQuery(id+"F8.wireOp",EDGE,"E122.filletArc"),sQuery(id+"F8.wireOp",EDGE,"E123.filletArc"),sQuery(id+"F8.wireOp",EDGE,"E125.MirrorCS"),sQuery(id+"F8.wireOp",EDGE,"E126.MirrorCS"),sQuery(id+"F8.wireOp",EDGE,"E127.MirrorCS"),sQuery(id+"F8.wireOp",EDGE,"E128.MirrorCS"),sQuery(id+"F8.wireOp",EDGE,"E129.MirrorCS"),sQuery(id+"F8.wireOp",EDGE,"E130.MirrorCS"),sQuery(id+"F8.wireOp",EDGE,"E131.MirrorCS"),sQuery(id+"F8.wireOp",EDGE,"E132.MirrorCS"),sQuery(id+"F8.wireOp",EDGE,"E133.MirrorCS"),sQuery(id+"F8.wireOp",EDGE,"E134.MirrorCS"),sQuery(id+"F8.wireOp",EDGE,"E135.MirrorCS"),sQuery(id+"F8.wireOp",EDGE,"E136.MirrorCS")])],"isStart":false});
            extrude(context, id + "F15", {"entities" : qUnion([Q0, Q1, Q2, Q3, Q4, Q5, Q6, Q7, Q8]), "operationType" : NewBodyOperationType.REMOVE, "endBound" : BoundingType.UP_TO_SURFACE, "oppositeDirection" : true, "endBoundEntityFace" : qUnion([Q9]), "depth" : 25.4 * mm});
        }
        {
            var Q0;
            {var subQ0=sQuery(id+"F9.wireOp",EDGE,"E168");Q0=makeQuery(id+"F9.imprint","IMPRINT",FACE,{"disambiguationData":[TD([[makeQuery(id+"F9.imprint","IMPRINT",EDGE,{"derivedFrom":subQ0}),-1.0]])]});}
            var Q1;
            {var subQ0=sQuery(id+"F9.wireOp",EDGE,"E193");Q1=makeQuery(id+"F9.imprint","IMPRINT",FACE,{"disambiguationData":[TD([[makeQuery(id+"F9.imprint","IMPRINT",EDGE,{"derivedFrom":subQ0}),-1.0]])]});}
            extrude(context, id + "F16", {"entities" : qUnion([Q0, Q1]), "operationType" : NewBodyOperationType.REMOVE, "depth" : 25.4 * mm});
        }
        {
            var Q0;
            Q0=qCreatedBy(makeId("Right.planeOp"),FACE);
            var sketch = newSketch(context, id + "F17", { "sketchPlane" : qUnion([Q0])});
            skLineSegment(sketch, "E260.0", {"start": v(-651.77, -620.9) * mm, "end": v(0, 508) * mm});
            skLineSegment(sketch, "E261.0", {"start": v(-638.02, -628.84) * mm, "end": v(-651.77, -620.9) * mm});
            skLineSegment(sketch, "E261.1", {"start": v(-231.62, 75.07) * mm, "end": v(-638.02, -628.84) * mm});
            skLineSegment(sketch, "E261.2", {"start": v(-245.37, 83) * mm, "end": v(-231.62, 75.07) * mm});
            skLineSegment(sketch, "E262.0", {"start": v(-231.62, 75.07) * mm, "end": v(-217.87, 67.13) * mm});
            skLineSegment(sketch, "E262.1", {"start": v(-217.87, 67.13) * mm, "end": v(-624.27, -636.77) * mm});
            skLineSegment(sketch, "E262.2", {"start": v(-624.27, -636.77) * mm, "end": v(-638.02, -628.84) * mm});
            skSolve(sketch);
        }
        {
            var Q0;
            {var subQ0=sQuery(id+"F17.wireOp",EDGE,"E261.0");Q0=makeQuery(id+"F17.imprint","IMPRINT",FACE,{"disambiguationData":[TD([[makeQuery(id+"F17.imprint","IMPRINT",EDGE,{"derivedFrom":subQ0}),-1.0]])]});}
            extrude(context, id + "F18", {"entities" : qUnion([Q0]), "depth" : (getVariable(context, 'panel_length')) * mm});
        }
        {
            var Q0;
            Q0=makeQuery(id+"F17.imprint","IMPRINT",FACE,{"disambiguationData":[TD([[makeQuery(id+"F17.imprint","IMPRINT",EDGE,{"derivedFrom":sQuery(id+"F17.wireOp",EDGE,"E261.1")}),1.0]])]});
            extrude(context, id + "F19", {"entities" : qUnion([Q0]), "depth" : (getVariable(context, 'panel_length')) * mm});
        }
        {
            var Q0;
            Q0=makeQuery(id+"F19.opExtrude","SWEPT_FACE",FACE,{"disambiguationData":[OSD([sQuery(id+"F17.wireOp",EDGE,"E262.1")])]});
            var sketch = newSketch(context, id + "F20", { "sketchPlane" : qUnion([Q0])});
            skLineSegment(sketch, "E263", {"start": v(-1219.2, -50.8) * mm, "end": v(-1219.2, -863.6) * mm});
            skLineSegment(sketch, "E264", {"start": v(-1219.2, -863.6) * mm, "end": v(0, -863.6) * mm});
            skLineSegment(sketch, "E265", {"start": v(0, -863.6) * mm, "end": v(0, -50.8) * mm});
            skLineSegment(sketch, "E266", {"start": v(0, -50.8) * mm, "end": v(-1219.2, -50.8) * mm});
            skLineSegment(sketch, "E267", {"start": v(-914.4, -50.8) * mm, "end": v(-914.4, -863.6) * mm, "construction": true});
            skLineSegment(sketch, "E268", {"start": v(-609.6, -863.6) * mm, "end": v(-609.6, -50.8) * mm, "construction": true});
            skLineSegment(sketch, "E269.right", {"start": v(-820.74, -50.8) * mm, "end": v(-820.74, -863.6) * mm, "construction": true});
            skLineSegment(sketch, "E270", {"start": v(-1008.06, -50.8) * mm, "end": v(-1008.06, -863.6) * mm, "construction": true});
            skLineSegment(sketch, "E271", {"start": v(-1219.2, -50.8) * mm, "end": v(-1219.2, -321.73) * mm, "construction": true});
            skLineSegment(sketch, "E272", {"start": v(-1219.2, -321.73) * mm, "end": v(-1219.2, -592.67) * mm, "construction": true});
            skLineSegment(sketch, "E273", {"start": v(-1219.2, -592.67) * mm, "end": v(-1219.2, -863.6) * mm, "construction": true});
            skLineSegment(sketch, "E274", {"start": v(-1219.2, -457.2) * mm, "end": v(0, -457.2) * mm, "construction": true});
            skLineSegment(sketch, "E275.MirrorCS", {"start": v(-406.4, -449.26) * mm, "end": v(-812.8, -449.26) * mm});
            skLineSegment(sketch, "E276", {"start": v(-1181.1, -88.9) * mm, "end": v(-1030.29, -88.9) * mm});
            skLineSegment(sketch, "E277.MirrorCS", {"start": v(-1181.1, -411.16) * mm, "end": v(-1030.29, -411.16) * mm});
            skLineSegment(sketch, "E278.2", {"start": v(-1181.1, -825.5) * mm, "end": v(-1030.29, -825.5) * mm});
            skLineSegment(sketch, "E279.trimOffspring", {"start": v(-798.51, -825.5) * mm, "end": v(-420.69, -825.5) * mm});
            skLineSegment(sketch, "E280.trimOffspring", {"start": v(-1030.29, -503.24) * mm, "end": v(-1181.1, -503.24) * mm});
            skLineSegment(sketch, "E281.trimOffspring", {"start": v(-1030.29, -503.24) * mm, "end": v(-1030.29, -825.5) * mm});
            skLineSegment(sketch, "E282.trimOffspring", {"start": v(-1181.1, -503.24) * mm, "end": v(-1181.1, -825.5) * mm});
            skLineSegment(sketch, "E283.trimOffspring", {"start": v(-1181.1, -88.9) * mm, "end": v(-1181.1, -411.16) * mm});
            skLineSegment(sketch, "E284.trimOffspring", {"start": v(-1030.29, -88.9) * mm, "end": v(-1030.29, -411.16) * mm});
            skLineSegment(sketch, "E285.trimOffspring", {"start": v(-798.51, -88.9) * mm, "end": v(-420.69, -88.9) * mm});
            skLineSegment(sketch, "E286.trimOffspring", {"start": v(-798.51, -88.9) * mm, "end": v(-798.51, -411.16) * mm});
            skLineSegment(sketch, "E287.trimOffspring", {"start": v(-798.51, -503.24) * mm, "end": v(-798.51, -825.5) * mm});
            skLineSegment(sketch, "E288.trimOffspring", {"start": v(-798.51, -411.16) * mm, "end": v(-420.69, -411.16) * mm});
            skLineSegment(sketch, "E289.trimOffspring", {"start": v(-420.69, -503.24) * mm, "end": v(-420.69, -825.5) * mm});
            skLineSegment(sketch, "E290.trimOffspring", {"start": v(-420.69, -503.24) * mm, "end": v(-798.51, -503.24) * mm});
            skLineSegment(sketch, "E291.trimOffspring", {"start": v(-420.69, -88.9) * mm, "end": v(-420.69, -411.16) * mm});
            skLineSegment(sketch, "E292", {"start": v(-836.61, -76.2) * mm, "end": v(-852.49, -76.2) * mm});
            skLineSegment(sketch, "E293", {"start": v(-836.61, -503.24) * mm, "end": v(-852.49, -503.24) * mm});
            skLineSegment(sketch, "E294", {"start": v(-836.61, -411.16) * mm, "end": v(-852.49, -411.16) * mm});
            skLineSegment(sketch, "E295.trimOffspring", {"start": v(-836.61, -503.24) * mm, "end": v(-836.61, -838.2) * mm});
            skLineSegment(sketch, "E296.trimOffspring", {"start": v(-852.49, -503.24) * mm, "end": v(-852.49, -838.2) * mm});
            skLineSegment(sketch, "E297.trimOffspring", {"start": v(-906.46, -411.16) * mm, "end": v(-922.34, -411.16) * mm});
            skLineSegment(sketch, "E298.trimOffspring", {"start": v(-922.34, -503.24) * mm, "end": v(-922.34, -838.2) * mm});
            skLineSegment(sketch, "E299.trimOffspring", {"start": v(-906.46, -503.24) * mm, "end": v(-906.46, -838.2) * mm});
            skLineSegment(sketch, "E300.trimOffspring", {"start": v(-976.31, -411.16) * mm, "end": v(-992.19, -411.16) * mm});
            skLineSegment(sketch, "E301.trimOffspring", {"start": v(-976.31, -503.24) * mm, "end": v(-976.31, -838.2) * mm});
            skLineSegment(sketch, "E302.trimOffspring", {"start": v(-992.19, -503.24) * mm, "end": v(-992.19, -838.2) * mm});
            skLineSegment(sketch, "E303.trimOffspring", {"start": v(-906.46, -503.24) * mm, "end": v(-922.34, -503.24) * mm});
            skLineSegment(sketch, "E304.trimOffspring", {"start": v(-976.31, -503.24) * mm, "end": v(-992.19, -503.24) * mm});
            skLineSegment(sketch, "E305.trimOffspring", {"start": v(-836.61, -76.2) * mm, "end": v(-836.61, -411.16) * mm});
            skLineSegment(sketch, "E306.trimOffspring", {"start": v(-852.49, -76.2) * mm, "end": v(-852.49, -411.16) * mm});
            skLineSegment(sketch, "E307.trimOffspring", {"start": v(-906.46, -76.2) * mm, "end": v(-922.34, -76.2) * mm});
            skLineSegment(sketch, "E308.trimOffspring", {"start": v(-906.46, -76.2) * mm, "end": v(-906.46, -411.16) * mm});
            skLineSegment(sketch, "E309.trimOffspring", {"start": v(-976.31, -76.2) * mm, "end": v(-992.19, -76.2) * mm});
            skLineSegment(sketch, "E310.trimOffspring", {"start": v(-922.34, -76.2) * mm, "end": v(-922.34, -411.16) * mm});
            skLineSegment(sketch, "E311.trimOffspring", {"start": v(-976.31, -76.2) * mm, "end": v(-976.31, -411.16) * mm});
            skLineSegment(sketch, "E312.trimOffspring", {"start": v(-992.19, -76.2) * mm, "end": v(-992.19, -411.16) * mm});
            skLineSegment(sketch, "E313", {"start": v(-836.61, -838.2) * mm, "end": v(-852.49, -838.2) * mm});
            skLineSegment(sketch, "E314", {"start": v(-906.46, -838.2) * mm, "end": v(-922.34, -838.2) * mm});
            skLineSegment(sketch, "E315", {"start": v(-976.31, -838.2) * mm, "end": v(-992.19, -838.2) * mm});
            skLineSegment(sketch, "E316", {"start": v(-852.49, -838.2) * mm, "end": v(-906.46, -838.2) * mm, "construction": true});
            skLineSegment(sketch, "E317", {"start": v(-922.34, -838.2) * mm, "end": v(-976.31, -838.2) * mm, "construction": true});
            skPoint(sketch, "E318", {"position": v(-914.4, -838.2) * mm});
            skLineSegment(sketch, "E319.MirrorCS", {"start": v(-312.74, -838.2) * mm, "end": v(-296.86, -838.2) * mm});
            skLineSegment(sketch, "E320.MirrorCS", {"start": v(-382.59, -503.24) * mm, "end": v(-366.71, -503.24) * mm});
            skLineSegment(sketch, "E321.MirrorCS", {"start": v(-382.59, -76.2) * mm, "end": v(-366.71, -76.2) * mm});
            skLineSegment(sketch, "E322.MirrorCS", {"start": v(-382.59, -411.16) * mm, "end": v(-366.71, -411.16) * mm});
            skLineSegment(sketch, "E323.MirrorCS", {"start": v(-242.89, -838.2) * mm, "end": v(-227.01, -838.2) * mm});
            skLineSegment(sketch, "E324.MirrorCS", {"start": v(-382.59, -838.2) * mm, "end": v(-366.71, -838.2) * mm});
            skLineSegment(sketch, "E325.MirrorCS", {"start": v(-242.89, -411.16) * mm, "end": v(-227.01, -411.16) * mm});
            skLineSegment(sketch, "E326.MirrorCS", {"start": v(-312.74, -411.16) * mm, "end": v(-296.86, -411.16) * mm});
            skLineSegment(sketch, "E327.MirrorCS", {"start": v(-312.74, -503.24) * mm, "end": v(-296.86, -503.24) * mm});
            skLineSegment(sketch, "E328.MirrorCS", {"start": v(-242.89, -503.24) * mm, "end": v(-227.01, -503.24) * mm});
            skLineSegment(sketch, "E329.MirrorCS", {"start": v(-312.74, -76.2) * mm, "end": v(-296.86, -76.2) * mm});
            skLineSegment(sketch, "E330.MirrorCS", {"start": v(-242.89, -76.2) * mm, "end": v(-227.01, -76.2) * mm});
            skLineSegment(sketch, "E331.MirrorCS", {"start": v(-296.86, -838.2) * mm, "end": v(-242.89, -838.2) * mm, "construction": true});
            skLineSegment(sketch, "E332.MirrorCS", {"start": v(-366.71, -838.2) * mm, "end": v(-312.74, -838.2) * mm, "construction": true});
            skLineSegment(sketch, "E333.MirrorCS", {"start": v(0, -50.8) * mm, "end": v(0, -321.73) * mm, "construction": true});
            skLineSegment(sketch, "E334.MirrorCS", {"start": v(0, -321.73) * mm, "end": v(0, -592.67) * mm, "construction": true});
            skLineSegment(sketch, "E335.MirrorCS", {"start": v(0, -592.67) * mm, "end": v(0, -863.6) * mm, "construction": true});
            skLineSegment(sketch, "E336.MirrorCS", {"start": v(-242.89, -76.2) * mm, "end": v(-242.89, -411.16) * mm});
            skLineSegment(sketch, "E337.MirrorCS", {"start": v(-38.1, -411.16) * mm, "end": v(-188.91, -411.16) * mm});
            skLineSegment(sketch, "E338.MirrorCS", {"start": v(-211.14, -50.8) * mm, "end": v(-211.14, -863.6) * mm, "construction": true});
            skLineSegment(sketch, "E339.MirrorCS", {"start": v(-38.1, -88.9) * mm, "end": v(-188.91, -88.9) * mm});
            skLineSegment(sketch, "E340.MirrorCS", {"start": v(-38.1, -503.24) * mm, "end": v(-38.1, -825.5) * mm});
            skLineSegment(sketch, "E341.MirrorCS", {"start": v(-38.1, -825.5) * mm, "end": v(-188.91, -825.5) * mm});
            skLineSegment(sketch, "E342.MirrorCS", {"start": v(-188.91, -503.24) * mm, "end": v(-38.1, -503.24) * mm});
            skLineSegment(sketch, "E343.MirrorCS", {"start": v(-188.91, -88.9) * mm, "end": v(-188.91, -411.16) * mm});
            skLineSegment(sketch, "E344.MirrorCS", {"start": v(-227.01, -76.2) * mm, "end": v(-227.01, -411.16) * mm});
            skLineSegment(sketch, "E345.MirrorCS", {"start": v(-188.91, -503.24) * mm, "end": v(-188.91, -825.5) * mm});
            skLineSegment(sketch, "E346.MirrorCS", {"start": v(-382.59, -503.24) * mm, "end": v(-382.59, -838.2) * mm});
            skLineSegment(sketch, "E347.MirrorCS", {"start": v(0, -50.8) * mm, "end": v(0, -863.6) * mm});
            skLineSegment(sketch, "E348.MirrorCS", {"start": v(-227.01, -503.24) * mm, "end": v(-227.01, -838.2) * mm});
            skLineSegment(sketch, "E349.MirrorCS", {"start": v(-366.71, -76.2) * mm, "end": v(-366.71, -411.16) * mm});
            skLineSegment(sketch, "E350.MirrorCS", {"start": v(-296.86, -76.2) * mm, "end": v(-296.86, -411.16) * mm});
            skLineSegment(sketch, "E351.MirrorCS", {"start": v(-312.74, -76.2) * mm, "end": v(-312.74, -411.16) * mm});
            skLineSegment(sketch, "E352.MirrorCS", {"start": v(-304.8, -50.8) * mm, "end": v(-304.8, -863.6) * mm, "construction": true});
            skLineSegment(sketch, "E353.MirrorCS", {"start": v(-312.74, -503.24) * mm, "end": v(-312.74, -838.2) * mm});
            skPoint(sketch, "E354.MirrorP", {"position": v(-304.8, -838.2) * mm});
            skLineSegment(sketch, "E355.MirrorCS", {"start": v(-366.71, -503.24) * mm, "end": v(-366.71, -838.2) * mm});
            skLineSegment(sketch, "E356.MirrorCS", {"start": v(-38.1, -88.9) * mm, "end": v(-38.1, -411.16) * mm});
            skLineSegment(sketch, "E357.MirrorCS", {"start": v(-296.86, -503.24) * mm, "end": v(-296.86, -838.2) * mm});
            skLineSegment(sketch, "E358.MirrorCS", {"start": v(-382.59, -76.2) * mm, "end": v(-382.59, -411.16) * mm});
            skLineSegment(sketch, "E359.MirrorCS", {"start": v(-242.89, -503.24) * mm, "end": v(-242.89, -838.2) * mm});
            skLineSegment(sketch, "E360", {"start": v(-812.8, -449.26) * mm, "end": v(-812.8, -465.14) * mm});
            skLineSegment(sketch, "E361.MirrorCS", {"start": v(-406.4, -465.14) * mm, "end": v(-812.8, -465.14) * mm});
            skLineSegment(sketch, "E362.MirrorCS", {"start": v(-406.4, -449.26) * mm, "end": v(-406.4, -465.14) * mm});
            skSolve(sketch);
        }
        {
            var Q0;
            Q0=makeQuery(id+"F20.imprint","IMPRINT",FACE,{"disambiguationData":[TD([[makeQuery(id+"F20.imprint","IMPRINT",EDGE,{"derivedFrom":sQuery(id+"F20.wireOp",EDGE,"E276")}),-1.0]])]});
            var Q1;
            Q1=makeQuery(id+"F20.imprint","IMPRINT",FACE,{"disambiguationData":[TD([[makeQuery(id+"F20.imprint","IMPRINT",EDGE,{"derivedFrom":sQuery(id+"F20.wireOp",EDGE,"E278.2")}),1.0]])]});
            var Q2;
            Q2=makeQuery(id+"F20.imprint","IMPRINT",FACE,{"disambiguationData":[TD([[makeQuery(id+"F20.imprint","IMPRINT",EDGE,{"derivedFrom":sQuery(id+"F20.wireOp",EDGE,"E279.trimOffspring")}),1.0]])]});
            var Q3;
            Q3=makeQuery(id+"F20.imprint","IMPRINT",FACE,{"disambiguationData":[TD([[makeQuery(id+"F20.imprint","IMPRINT",EDGE,{"derivedFrom":sQuery(id+"F20.wireOp",EDGE,"E285.trimOffspring")}),-1.0]])]});
            var Q4;
            Q4=makeQuery(id+"F20.imprint","IMPRINT",FACE,{"disambiguationData":[TD([[makeQuery(id+"F20.imprint","IMPRINT",EDGE,{"derivedFrom":sQuery(id+"F20.wireOp",EDGE,"E337.MirrorCS")}),-1.0]])]});
            var Q5;
            Q5=makeQuery(id+"F20.imprint","IMPRINT",FACE,{"disambiguationData":[TD([[makeQuery(id+"F20.imprint","IMPRINT",EDGE,{"derivedFrom":sQuery(id+"F20.wireOp",EDGE,"E340.MirrorCS")}),-1.0]])]});
            var Q6;
            Q6=makeQuery(id+"F20.imprint","IMPRINT",FACE,{"disambiguationData":[TD([[makeQuery(id+"F20.imprint","IMPRINT",EDGE,{"derivedFrom":sQuery(id+"F20.wireOp",EDGE,"E323.MirrorCS")}),1.0]])]});
            var Q7;
            Q7=makeQuery(id+"F20.imprint","IMPRINT",FACE,{"disambiguationData":[TD([[makeQuery(id+"F20.imprint","IMPRINT",EDGE,{"derivedFrom":sQuery(id+"F20.wireOp",EDGE,"E319.MirrorCS")}),1.0]])]});
            var Q8;
            Q8=makeQuery(id+"F20.imprint","IMPRINT",FACE,{"disambiguationData":[TD([[makeQuery(id+"F20.imprint","IMPRINT",EDGE,{"derivedFrom":sQuery(id+"F20.wireOp",EDGE,"E320.MirrorCS")}),-1.0]])]});
            var Q9;
            Q9=makeQuery(id+"F20.imprint","IMPRINT",FACE,{"disambiguationData":[TD([[makeQuery(id+"F20.imprint","IMPRINT",EDGE,{"derivedFrom":sQuery(id+"F20.wireOp",EDGE,"E301.trimOffspring")}),-1.0]])]});
            var Q10;
            Q10=makeQuery(id+"F20.imprint","IMPRINT",FACE,{"disambiguationData":[TD([[makeQuery(id+"F20.imprint","IMPRINT",EDGE,{"derivedFrom":sQuery(id+"F20.wireOp",EDGE,"E298.trimOffspring")}),1.0]])]});
            var Q11;
            Q11=makeQuery(id+"F20.imprint","IMPRINT",FACE,{"disambiguationData":[TD([[makeQuery(id+"F20.imprint","IMPRINT",EDGE,{"derivedFrom":sQuery(id+"F20.wireOp",EDGE,"E293")}),1.0]])]});
            var Q12;
            Q12=makeQuery(id+"F20.imprint","IMPRINT",FACE,{"disambiguationData":[TD([[makeQuery(id+"F20.imprint","IMPRINT",EDGE,{"derivedFrom":sQuery(id+"F20.wireOp",EDGE,"E300.trimOffspring")}),-1.0]])]});
            var Q13;
            Q13=makeQuery(id+"F20.imprint","IMPRINT",FACE,{"disambiguationData":[TD([[makeQuery(id+"F20.imprint","IMPRINT",EDGE,{"derivedFrom":sQuery(id+"F20.wireOp",EDGE,"E297.trimOffspring")}),-1.0]])]});
            var Q14;
            Q14=makeQuery(id+"F20.imprint","IMPRINT",FACE,{"disambiguationData":[TD([[makeQuery(id+"F20.imprint","IMPRINT",EDGE,{"derivedFrom":sQuery(id+"F20.wireOp",EDGE,"E292")}),1.0]])]});
            var Q15;
            Q15=makeQuery(id+"F20.imprint","IMPRINT",FACE,{"disambiguationData":[TD([[makeQuery(id+"F20.imprint","IMPRINT",EDGE,{"derivedFrom":sQuery(id+"F20.wireOp",EDGE,"E275.MirrorCS")}),1.0]])]});
            var Q16;
            Q16=makeQuery(id+"F20.imprint","IMPRINT",FACE,{"disambiguationData":[TD([[makeQuery(id+"F20.imprint","IMPRINT",EDGE,{"derivedFrom":sQuery(id+"F20.wireOp",EDGE,"E321.MirrorCS")}),-1.0]])]});
            var Q17;
            Q17=makeQuery(id+"F20.imprint","IMPRINT",FACE,{"disambiguationData":[TD([[makeQuery(id+"F20.imprint","IMPRINT",EDGE,{"derivedFrom":sQuery(id+"F20.wireOp",EDGE,"E326.MirrorCS")}),1.0]])]});
            var Q18;
            Q18=makeQuery(id+"F20.imprint","IMPRINT",FACE,{"disambiguationData":[TD([[makeQuery(id+"F20.imprint","IMPRINT",EDGE,{"derivedFrom":sQuery(id+"F20.wireOp",EDGE,"E325.MirrorCS")}),1.0]])]});
            var Q19;
            Q19=makeQuery(id+"F19.opExtrude","SWEPT_FACE",FACE,{"disambiguationData":[OSD([sQuery(id+"F17.wireOp",EDGE,"E261.1")])]});
            extrude(context, id + "F21", {"entities" : qUnion([Q0, Q1, Q2, Q3, Q4, Q5, Q6, Q7, Q8, Q9, Q10, Q11, Q12, Q13, Q14, Q15, Q16, Q17, Q18]), "operationType" : NewBodyOperationType.REMOVE, "endBound" : BoundingType.UP_TO_SURFACE, "oppositeDirection" : true, "endBoundEntityFace" : qUnion([Q19]), "depth" : 25.4 * mm});
        }
        {
            var Q0;
            Q0=qCreatedBy(makeId("Right.planeOp"),FACE);
            var sketch = newSketch(context, id + "F22", { "sketchPlane" : qUnion([Q0])});
            skLineSegment(sketch, "E363.0.1", {"start": v(-212.37, 63.96) * mm, "end": v(-574.32, -562.96) * mm, "construction": true});
            skLineSegment(sketch, "E363.1.0", {"start": v(-217.87, 67.13) * mm, "end": v(-231.62, 75.07) * mm, "construction": true});
            skLineSegment(sketch, "E363.1.1", {"start": v(-231.62, 75.07) * mm, "end": v(-638.02, -628.84) * mm, "construction": true});
            skLineSegment(sketch, "E363.1.2", {"start": v(-638.02, -628.84) * mm, "end": v(-624.27, -636.77) * mm, "construction": true});
            skLineSegment(sketch, "E363.1.3", {"start": v(-624.27, -636.77) * mm, "end": v(-217.87, 67.13) * mm, "construction": true});
            skLineSegment(sketch, "E363.2.0", {"start": v(-429.78, -382.45) * mm, "end": v(-544.08, -580.42) * mm});
            skArc(sketch, "E363.2.1", {"start": v(-544.08, -580.42) * mm, "mid": v(-540.6, -593.43) * mm, "end": v(-527.58, -589.95) * mm});
            skLineSegment(sketch, "E363.2.2", {"start": v(-527.58, -589.95) * mm, "end": v(-413.28, -391.97) * mm});
            skArc(sketch, "E363.2.3", {"start": v(-413.28, -391.97) * mm, "mid": v(-416.77, -378.96) * mm, "end": v(-429.78, -382.45) * mm});
            skCircle(sketch, "E363.3.0", {"center": v(-218.33, -35.26) * mm, "radius": 9.53 * mm});
            skCircle(sketch, "E364.0", {"center": v(-535.83, -585.18) * mm, "radius": 44.45 * mm, "construction": true});
            skCircle(sketch, "E365.0", {"center": v(-218.33, -35.26) * mm, "radius": 44.45 * mm, "construction": true});
            skLineSegment(sketch, "E366", {"start": v(-244.32, 53.07) * mm, "end": v(-230.57, 45.13) * mm});
            skLineSegment(sketch, "E367", {"start": v(-230.57, 45.13) * mm, "end": v(-185.2, -5.63) * mm});
            skLineSegment(sketch, "E368", {"start": v(-179.84, -57.48) * mm, "end": v(-497.34, -607.4) * mm});
            skLineSegment(sketch, "E369", {"start": v(-625.32, -606.84) * mm, "end": v(-611.57, -614.78) * mm});
            skLineSegment(sketch, "E370", {"start": v(-611.57, -614.78) * mm, "end": v(-544.92, -628.7) * mm});
            skLineSegment(sketch, "E371", {"start": v(-244.32, 53.07) * mm, "end": v(-411.8, -237.01) * mm});
            skArc(sketch, "E372", {"start": v(-179.84, -57.48) * mm, "mid": v(-174.12, -30.7) * mm, "end": v(-185.2, -5.63) * mm});
            skArc(sketch, "E373", {"start": v(-544.92, -628.7) * mm, "mid": v(-517.68, -625.76) * mm, "end": v(-497.34, -607.4) * mm});
            skCircle(sketch, "E374", {"center": v(-421.53, -387.21) * mm, "radius": 44.45 * mm, "construction": true});
            skLineSegment(sketch, "E375", {"start": v(-421.53, -387.21) * mm, "end": v(-380.9, -316.82) * mm, "construction": true});
            skCircle(sketch, "E376", {"center": v(-380.9, -316.82) * mm, "radius": 25.4 * mm});
            skLineSegment(sketch, "E377", {"start": v(-380.9, -316.82) * mm, "end": v(-340.25, -246.43) * mm, "construction": true});
            skCircle(sketch, "E378", {"center": v(-340.25, -246.43) * mm, "radius": 25.4 * mm});
            skLineSegment(sketch, "E379", {"start": v(-340.25, -246.43) * mm, "end": v(-299.61, -176.04) * mm, "construction": true});
            skCircle(sketch, "E380", {"center": v(-299.61, -176.04) * mm, "radius": 25.4 * mm});
            skLineSegment(sketch, "E381", {"start": v(-299.61, -176.04) * mm, "end": v(-258.97, -105.65) * mm, "construction": true});
            skLineSegment(sketch, "E382", {"start": v(-218.33, -35.26) * mm, "end": v(-258.97, -105.65) * mm, "construction": true});
            skCircle(sketch, "E383", {"center": v(-258.97, -105.65) * mm, "radius": 25.4 * mm});
            skLineSegment(sketch, "E384.0", {"start": v(-457.84, -316.75) * mm, "end": v(-444.1, -324.7) * mm});
            skLineSegment(sketch, "E385.0", {"start": v(-411.8, -237.01) * mm, "end": v(-398.06, -244.95) * mm});
            skLineSegment(sketch, "E386", {"start": v(-398.06, -244.95) * mm, "end": v(-444.1, -324.7) * mm});
            skLineSegment(sketch, "E387.trimOffspring", {"start": v(-457.84, -316.75) * mm, "end": v(-625.32, -606.84) * mm});
            skSolve(sketch);
        }
        {
            var Q0;
            Q0=makeQuery(id+"F22.imprint","IMPRINT",FACE,{"disambiguationData":[TD([[makeQuery(id+"F22.imprint","IMPRINT",EDGE,{"derivedFrom":sQuery(id+"F22.wireOp",EDGE,"E363.2.0")}),-1.0]])]});
            extrude(context, id + "F23", {"entities" : qUnion([Q0]), "depth" : (getVariable(context, 'ply_thk')) * mm});
        }
        {
            var Q0;
            Q0=makeQuery(id+"F20.imprint","IMPRINT",FACE,{"disambiguationData":[TD([[makeQuery(id+"F20.imprint","IMPRINT",EDGE,{"derivedFrom":sQuery(id+"F20.wireOp",EDGE,"E275.MirrorCS")}),1.0]])]});
            extrude(context, id + "F24", {"entities" : qUnion([Q0]), "oppositeDirection" : true, "depth" : 76.2 * mm});
        }
        {
            var Q0;
            Q0=makeQuery(id+"F24.opExtrude","SWEPT_FACE",FACE,{"disambiguationData":[OSD([sQuery(id+"F20.wireOp",EDGE,"E361.MirrorCS")])]});
            var sketch = newSketch(context, id + "F25", { "sketchPlane" : qUnion([Q0])});
            skLineSegment(sketch, "E388.0.0", {"start": v(812.8, 222.25) * mm, "end": v(406.4, 222.25) * mm});
            skLineSegment(sketch, "E388.0.1", {"start": v(406.4, 222.25) * mm, "end": v(406.4, 238.13) * mm});
            skLineSegment(sketch, "E388.0.2", {"start": v(448.32, 298.45) * mm, "end": v(770.88, 298.45) * mm});
            skArc(sketch, "E389", {"start": v(411.24, 269.1) * mm, "mid": v(408.22, 253.71) * mm, "end": v(406.4, 238.13) * mm});
            skPoint(sketch, "E390.orphan", {"position": v(406.4, 298.45) * mm});
            skPoint(sketch, "E391.visualSharp", {"position": v(420.56, 298.45) * mm});
            skArc(sketch, "E391.filletArc", {"start": v(448.32, 298.45) * mm, "mid": v(424.68, 290.23) * mm, "end": v(411.24, 269.1) * mm});
            skLineSegment(sketch, "E392", {"start": v(609.6, 222.25) * mm, "end": v(609.6, 298.45) * mm, "construction": true});
            skArc(sketch, "E393.MirrorCS", {"start": v(807.96, 269.1) * mm, "mid": v(810.98, 253.71) * mm, "end": v(812.8, 238.13) * mm});
            skArc(sketch, "E394.MirrorCS", {"start": v(770.88, 298.45) * mm, "mid": v(794.52, 290.23) * mm, "end": v(807.96, 269.1) * mm});
            skLineSegment(sketch, "E395.MirrorCS", {"start": v(812.8, 222.25) * mm, "end": v(812.8, 238.13) * mm});
            skPoint(sketch, "E396.orphan", {"position": v(812.8, 298.45) * mm});
            skCircle(sketch, "E397.MirrorC", {"center": v(448.32, 260.35) * mm, "radius": 20.32 * mm});
            skCircle(sketch, "E398.1.0.0", {"center": v(502.08, 260.35) * mm, "radius": 20.32 * mm});
            skCircle(sketch, "E398.2.0.0", {"center": v(555.84, 260.35) * mm, "radius": 20.32 * mm});
            skLineSegment(sketch, "E398.direction1", {"start": v(448.32, 260.35) * mm, "end": v(502.08, 260.35) * mm, "construction": true});
            skPoint(sketch, "E399", {"position": v(609.6, 260.35) * mm});
            skCircle(sketch, "E400.0.3.0", {"center": v(609.6, 260.35) * mm, "radius": 20.32 * mm});
            skCircle(sketch, "E400.0.4.0", {"center": v(663.36, 260.35) * mm, "radius": 20.32 * mm});
            skCircle(sketch, "E400.0.5.0", {"center": v(717.12, 260.35) * mm, "radius": 20.32 * mm});
            skCircle(sketch, "E401.0.6.0", {"center": v(770.88, 260.35) * mm, "radius": 20.32 * mm});
            skSolve(sketch);
        }
        {
            var Q0;
            Q0=makeQuery(id+"F25.imprint","IMPRINT",FACE,{"disambiguationData":[TD([[makeQuery(id+"F25.imprint","IMPRINT",EDGE,{"derivedFrom":sQuery(id+"F25.wireOp",EDGE,"E388.0.0")}),1.0]])]});
            extrude(context, id + "F26", {"entities" : qUnion([Q0]), "operationType" : NewBodyOperationType.INTERSECT, "oppositeDirection" : true, "depth" : 25.4 * mm});
        }
    });
